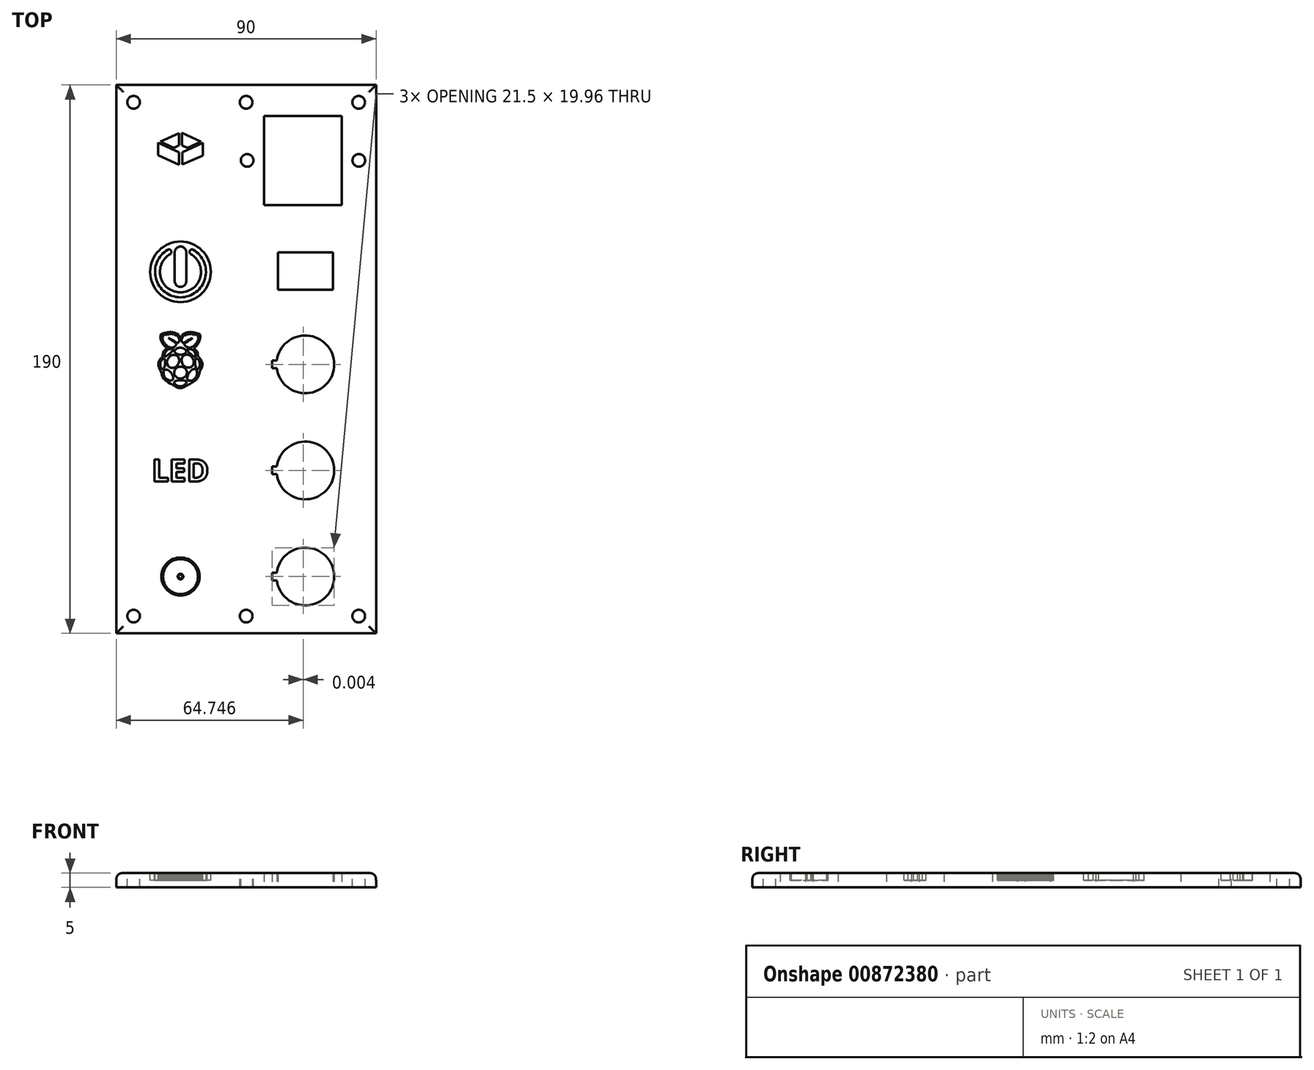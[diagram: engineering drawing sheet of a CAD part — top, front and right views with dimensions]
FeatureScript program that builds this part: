
annotation { "Feature Type Name" : "Feature", "Feature Type Description" : "" }
export const myFeature = defineFeature(function(context is Context, id is Id, definition is map)
    precondition{}
    {
        {
            var Q0;
            Q0=qCreatedBy(makeId("Top.planeOp"),FACE);
            var sketch = newSketch(context, id + "F0", { "sketchPlane" : qUnion([Q0])});
            skLineSegment(sketch, "E0.bottom", {"start": v(-22.25, -95) * mm, "end": v(-22.25, 95) * mm});
            skLineSegment(sketch, "E0.top", {"start": v(67.75, -95) * mm, "end": v(67.75, 95) * mm});
            skLineSegment(sketch, "E0.left", {"start": v(-22.25, -95) * mm, "end": v(67.75, -95) * mm});
            skLineSegment(sketch, "E0.right", {"start": v(-22.25, 95) * mm, "end": v(67.75, 95) * mm});
            skPoint(sketch, "E0.middle", {"position": v(31.26, -2.25) * mm});
            skLineSegment(sketch, "E1.bottom", {"start": v(55.89, 53.44) * mm, "end": v(29, 53.44) * mm});
            skLineSegment(sketch, "E1.top", {"start": v(55.89, 84.3) * mm, "end": v(29, 84.3) * mm});
            skLineSegment(sketch, "E1.left", {"start": v(55.89, 53.44) * mm, "end": v(55.89, 84.3) * mm});
            skLineSegment(sketch, "E1.right", {"start": v(29, 53.44) * mm, "end": v(29, 84.3) * mm});
            skLineSegment(sketch, "E2.bottom", {"start": v(33.81, 24.03) * mm, "end": v(33.81, 36.97) * mm});
            skLineSegment(sketch, "E2.top", {"start": v(52.81, 24.03) * mm, "end": v(52.81, 36.97) * mm});
            skLineSegment(sketch, "E2.left", {"start": v(33.81, 24.03) * mm, "end": v(52.81, 24.03) * mm});
            skLineSegment(sketch, "E2.right", {"start": v(33.81, 36.97) * mm, "end": v(52.81, 36.97) * mm});
            skPoint(sketch, "E3", {"position": v(61.79, 68.87) * mm});
            skPoint(sketch, "E4.endSnap0", {"position": v(42.44, 53.44) * mm});
            skPoint(sketch, "E5.MirrorP", {"position": v(23.1, 68.87) * mm});
            skArc(sketch, "E6", {"start": v(33.34, -3.11) * mm, "mid": v(53.25, -1.79) * mm, "end": v(33.34, -0.46) * mm});
            skLineSegment(sketch, "E7.top", {"start": v(33.34, -3.11) * mm, "end": v(31.75, -3.11) * mm});
            skLineSegment(sketch, "E8.MirrorCS", {"start": v(33.34, -0.46) * mm, "end": v(31.75, -0.46) * mm});
            skPoint(sketch, "E9.orphan", {"position": v(33.34, -0.46) * mm});
            skPoint(sketch, "E10.orphan", {"position": v(31.75, -0.46) * mm});
            skPoint(sketch, "E7.right.start.orphan", {"position": v(31.75, -1.79) * mm});
            skLineSegment(sketch, "E11", {"start": v(31.75, -0.46) * mm, "end": v(31.75, -3.11) * mm});
            skArc(sketch, "E12", {"start": v(33.34, -39.87) * mm, "mid": v(53.25, -38.54) * mm, "end": v(33.34, -37.22) * mm});
            skLineSegment(sketch, "E13.top", {"start": v(33.34, -39.87) * mm, "end": v(31.75, -39.87) * mm});
            skLineSegment(sketch, "E14.MirrorCS", {"start": v(33.34, -37.22) * mm, "end": v(31.75, -37.22) * mm});
            skLineSegment(sketch, "E15", {"start": v(31.75, -37.22) * mm, "end": v(31.75, -39.87) * mm});
            skArc(sketch, "E16", {"start": v(33.33, -76.62) * mm, "mid": v(53.25, -75.3) * mm, "end": v(33.33, -73.97) * mm});
            skLineSegment(sketch, "E17.top", {"start": v(33.33, -76.62) * mm, "end": v(31.75, -76.62) * mm});
            skLineSegment(sketch, "E18.MirrorCS", {"start": v(33.33, -73.97) * mm, "end": v(31.75, -73.97) * mm});
            skLineSegment(sketch, "E19", {"start": v(31.75, -73.97) * mm, "end": v(31.75, -76.62) * mm});
            skSolve(sketch);
        }
        {
            var Q0;
            Q0 = qSketchRegion(id + "F0", true);
            extrude(context, id + "F1", {"entities" : qUnion([Q0]), "depth" : 5 * mm, "offsetDistance" : 25 * mm});
        }
        {
            var Q0;
            Q0=makeQuery(id+"F1.opExtrude","CAP_FACE",FACE,{"disambiguationData":[OSD([sQuery(id+"F0.wireOp",EDGE,"E0.bottom"),sQuery(id+"F0.wireOp",EDGE,"E0.top"),sQuery(id+"F0.wireOp",EDGE,"E0.left"),sQuery(id+"F0.wireOp",EDGE,"E0.right"),sQuery(id+"F0.wireOp",EDGE,"E1.bottom"),sQuery(id+"F0.wireOp",EDGE,"E1.top"),sQuery(id+"F0.wireOp",EDGE,"E1.left"),sQuery(id+"F0.wireOp",EDGE,"E1.right"),sQuery(id+"F0.wireOp",EDGE,"E2.bottom"),sQuery(id+"F0.wireOp",EDGE,"E2.top"),sQuery(id+"F0.wireOp",EDGE,"E2.left"),sQuery(id+"F0.wireOp",EDGE,"E2.right"),sQuery(id+"F0.wireOp",EDGE,"E6"),sQuery(id+"F0.wireOp",EDGE,"E7.top"),sQuery(id+"F0.wireOp",EDGE,"E8.MirrorCS"),sQuery(id+"F0.wireOp",EDGE,"E11"),sQuery(id+"F0.wireOp",EDGE,"E12"),sQuery(id+"F0.wireOp",EDGE,"E13.top"),sQuery(id+"F0.wireOp",EDGE,"E14.MirrorCS"),sQuery(id+"F0.wireOp",EDGE,"E15"),sQuery(id+"F0.wireOp",EDGE,"E16"),sQuery(id+"F0.wireOp",EDGE,"E17.top"),sQuery(id+"F0.wireOp",EDGE,"E18.MirrorCS"),sQuery(id+"F0.wireOp",EDGE,"E19")])],"isStart":false});
            var sketch = newSketch(context, id + "F2", { "sketchPlane" : qUnion([Q0])});
            skPoint(sketch, "E20", {"position": v(61.79, 68.87) * mm});
            skPoint(sketch, "E21.MirrorP", {"position": v(23.1, 68.87) * mm});
            skCircle(sketch, "E22", {"center": v(0, 30.27) * mm, "radius": 11.5 * mm});
            skCircle(sketch, "E23", {"center": v(0, 30.27) * mm, "radius": 10.5 * mm});
            skArc(sketch, "E24", {"start": v(-4.42, 37.91) * mm, "mid": v(0, 21.44) * mm, "end": v(4.42, 37.91) * mm});
            skArc(sketch, "E25", {"start": v(-3.56, 36.44) * mm, "mid": v(0, 23.15) * mm, "end": v(3.56, 36.44) * mm});
            skPoint(sketch, "E26.orphan", {"position": v(0, 31.77) * mm});
            skArc(sketch, "E27", {"start": v(-4.42, 37.91) * mm, "mid": v(-3.25, 37.6) * mm, "end": v(-3.56, 36.44) * mm});
            skArc(sketch, "E28", {"start": v(4.42, 37.91) * mm, "mid": v(3.25, 37.6) * mm, "end": v(3.56, 36.44) * mm});
            skLineSegment(sketch, "E29.left", {"start": v(-2, 37.03) * mm, "end": v(-2, 27.03) * mm});
            skLineSegment(sketch, "E30.MirrorCS", {"start": v(2, 37.03) * mm, "end": v(2, 27.03) * mm});
            skArc(sketch, "E31", {"start": v(-2, 37.03) * mm, "mid": v(0, 39.03) * mm, "end": v(2, 37.03) * mm});
            skArc(sketch, "E32", {"start": v(2, 27.03) * mm, "mid": v(0, 25.03) * mm, "end": v(-2, 27.03) * mm});
            skCircle(sketch, "E33", {"center": v(0, -75.3) * mm, "radius": 0.97 * mm});
            skCircle(sketch, "E34", {"center": v(0, -75.3) * mm, "radius": 0.68 * mm});
            skCircle(sketch, "E35", {"center": v(0, -75.3) * mm, "radius": 6.05 * mm});
            skLineSegment(sketch, "E36", {"start": v(-0.85, -75.76) * mm, "end": v(-4.24, -78.57) * mm});
            skArc(sketch, "E37", {"start": v(-4.24, -78.57) * mm, "mid": v(-4.24, -79.53) * mm, "end": v(-3.28, -79.53) * mm});
            skLineSegment(sketch, "E38", {"start": v(-3.28, -79.53) * mm, "end": v(-0.47, -76.14) * mm});
            skLineSegment(sketch, "E39", {"start": v(-0.85, -74.83) * mm, "end": v(-4.24, -72.01) * mm});
            skArc(sketch, "E40", {"start": v(-4.24, -72.01) * mm, "mid": v(-4.24, -71.05) * mm, "end": v(-3.28, -71.05) * mm});
            skLineSegment(sketch, "E41", {"start": v(-3.28, -71.05) * mm, "end": v(-0.47, -74.44) * mm});
            skLineSegment(sketch, "E42", {"start": v(0.47, -76.14) * mm, "end": v(3.28, -79.53) * mm});
            skArc(sketch, "E43", {"start": v(3.28, -79.53) * mm, "mid": v(4.24, -79.53) * mm, "end": v(4.24, -78.57) * mm});
            skLineSegment(sketch, "E44", {"start": v(4.24, -78.57) * mm, "end": v(0.85, -75.76) * mm});
            skLineSegment(sketch, "E45", {"start": v(0.85, -74.83) * mm, "end": v(4.24, -72.01) * mm});
            skArc(sketch, "E46", {"start": v(4.24, -72.01) * mm, "mid": v(4.24, -71.05) * mm, "end": v(3.28, -71.05) * mm});
            skLineSegment(sketch, "E47", {"start": v(3.28, -71.05) * mm, "end": v(0.47, -74.44) * mm});
            skCircle(sketch, "E48", {"center": v(0, -75.3) * mm, "radius": 6.34 * mm});
            skText(sketch, "E49", { "text": "LED", "fontName": "OpenSans-Bold.ttf"});
            skLineSegment(sketch, "E50", {"start": v(0.77, -9.9) * mm, "end": v(0.41, -9.96) * mm});
            skLineSegment(sketch, "E51", {"start": v(0.41, -9.96) * mm, "end": v(0.04, -9.98) * mm});
            skLineSegment(sketch, "E52", {"start": v(2.22, -9.1) * mm, "end": v(1.83, -9.4) * mm});
            skLineSegment(sketch, "E53", {"start": v(1.83, -9.4) * mm, "end": v(1.43, -9.65) * mm});
            skLineSegment(sketch, "E54", {"start": v(1.43, -9.65) * mm, "end": v(0.77, -9.9) * mm});
            skLineSegment(sketch, "E55", {"start": v(2.71, -8.8) * mm, "end": v(2.41, -8.95) * mm});
            skLineSegment(sketch, "E56", {"start": v(2.41, -8.95) * mm, "end": v(2.22, -9.1) * mm});
            skLineSegment(sketch, "E57", {"start": v(3.97, -8.09) * mm, "end": v(3.25, -8.54) * mm});
            skLineSegment(sketch, "E58", {"start": v(3.25, -8.54) * mm, "end": v(2.71, -8.8) * mm});
            skLineSegment(sketch, "E59", {"start": v(4.54, -7.73) * mm, "end": v(4.42, -7.8) * mm});
            skLineSegment(sketch, "E60", {"start": v(4.42, -7.8) * mm, "end": v(4.25, -7.9) * mm});
            skLineSegment(sketch, "E61", {"start": v(4.25, -7.9) * mm, "end": v(3.97, -8.09) * mm});
            skLineSegment(sketch, "E62", {"start": v(5.46, -7.06) * mm, "end": v(5.2, -7.3) * mm});
            skLineSegment(sketch, "E63", {"start": v(5.2, -7.3) * mm, "end": v(4.95, -7.5) * mm});
            skLineSegment(sketch, "E64", {"start": v(4.95, -7.5) * mm, "end": v(4.54, -7.73) * mm});
            skLineSegment(sketch, "E65", {"start": v(6.35, -5.42) * mm, "end": v(6.2, -5.93) * mm});
            skLineSegment(sketch, "E66", {"start": v(6.2, -5.93) * mm, "end": v(5.98, -6.4) * mm});
            skLineSegment(sketch, "E67", {"start": v(5.98, -6.4) * mm, "end": v(5.74, -6.74) * mm});
            skLineSegment(sketch, "E68", {"start": v(5.74, -6.74) * mm, "end": v(5.46, -7.06) * mm});
            skLineSegment(sketch, "E69", {"start": v(6.54, -4.76) * mm, "end": v(6.42, -5.15) * mm});
            skLineSegment(sketch, "E70", {"start": v(6.42, -5.15) * mm, "end": v(6.35, -5.42) * mm});
            skLineSegment(sketch, "E71", {"start": v(6.74, -4.12) * mm, "end": v(6.7, -4.26) * mm});
            skLineSegment(sketch, "E72", {"start": v(6.7, -4.26) * mm, "end": v(6.64, -4.45) * mm});
            skLineSegment(sketch, "E73", {"start": v(6.64, -4.45) * mm, "end": v(6.54, -4.76) * mm});
            skLineSegment(sketch, "E74", {"start": v(6.97, -3.64) * mm, "end": v(6.88, -3.78) * mm});
            skLineSegment(sketch, "E75", {"start": v(6.88, -3.78) * mm, "end": v(6.82, -3.9) * mm});
            skLineSegment(sketch, "E76", {"start": v(6.82, -3.9) * mm, "end": v(6.74, -4.12) * mm});
            skLineSegment(sketch, "E77", {"start": v(7.5, -2.58) * mm, "end": v(7.39, -2.89) * mm});
            skLineSegment(sketch, "E78", {"start": v(7.39, -2.89) * mm, "end": v(7.24, -3.2) * mm});
            skLineSegment(sketch, "E79", {"start": v(7.24, -3.2) * mm, "end": v(7.11, -3.44) * mm});
            skLineSegment(sketch, "E80", {"start": v(7.11, -3.44) * mm, "end": v(6.97, -3.64) * mm});
            skLineSegment(sketch, "E81", {"start": v(7.5, -1.16) * mm, "end": v(7.55, -1.53) * mm});
            skLineSegment(sketch, "E82", {"start": v(7.55, -1.53) * mm, "end": v(7.57, -1.97) * mm});
            skLineSegment(sketch, "E83", {"start": v(7.57, -1.97) * mm, "end": v(7.54, -2.3) * mm});
            skLineSegment(sketch, "E84", {"start": v(7.54, -2.3) * mm, "end": v(7.5, -2.58) * mm});
            skLineSegment(sketch, "E85", {"start": v(7.13, -0.28) * mm, "end": v(7.36, -0.76) * mm});
            skLineSegment(sketch, "E86", {"start": v(7.36, -0.76) * mm, "end": v(7.5, -1.16) * mm});
            skLineSegment(sketch, "E87", {"start": v(6.4, 0.55) * mm, "end": v(6.6, 0.38) * mm});
            skLineSegment(sketch, "E88", {"start": v(6.6, 0.38) * mm, "end": v(6.83, 0.13) * mm});
            skLineSegment(sketch, "E89", {"start": v(6.83, 0.13) * mm, "end": v(7, -0.08) * mm});
            skLineSegment(sketch, "E90", {"start": v(7, -0.08) * mm, "end": v(7.13, -0.28) * mm});
            skLineSegment(sketch, "E91", {"start": v(6.11, 1.25) * mm, "end": v(6.14, 0.96) * mm});
            skLineSegment(sketch, "E92", {"start": v(6.14, 0.96) * mm, "end": v(6.2, 0.76) * mm});
            skLineSegment(sketch, "E93", {"start": v(6.2, 0.76) * mm, "end": v(6.4, 0.55) * mm});
            skLineSegment(sketch, "E94", {"start": v(4.65, 3.74) * mm, "end": v(5.12, 3.4) * mm});
            skLineSegment(sketch, "E95", {"start": v(5.12, 3.4) * mm, "end": v(5.5, 3) * mm});
            skLineSegment(sketch, "E96", {"start": v(5.5, 3) * mm, "end": v(5.79, 2.54) * mm});
            skLineSegment(sketch, "E97", {"start": v(5.79, 2.54) * mm, "end": v(6.01, 1.93) * mm});
            skLineSegment(sketch, "E98", {"start": v(6.01, 1.93) * mm, "end": v(6.11, 1.25) * mm});
            skLineSegment(sketch, "E99", {"start": v(4.5, 3.84) * mm, "end": v(4.65, 3.74) * mm});
            skLineSegment(sketch, "E100", {"start": v(4.69, 3.93) * mm, "end": v(4.5, 3.84) * mm});
            skLineSegment(sketch, "E101", {"start": v(5.03, 4.27) * mm, "end": v(4.9, 4.06) * mm});
            skLineSegment(sketch, "E102", {"start": v(4.9, 4.06) * mm, "end": v(4.69, 3.93) * mm});
            skLineSegment(sketch, "E103", {"start": v(5.22, 4.4) * mm, "end": v(5.08, 4.32) * mm});
            skLineSegment(sketch, "E104", {"start": v(5.08, 4.32) * mm, "end": v(5.03, 4.27) * mm});
            skLineSegment(sketch, "E105", {"start": v(5.66, 4.82) * mm, "end": v(5.59, 4.67) * mm});
            skLineSegment(sketch, "E106", {"start": v(5.59, 4.67) * mm, "end": v(5.47, 4.54) * mm});
            skLineSegment(sketch, "E107", {"start": v(5.47, 4.54) * mm, "end": v(5.22, 4.4) * mm});
            skLineSegment(sketch, "E108", {"start": v(5.79, 5) * mm, "end": v(5.7, 4.92) * mm});
            skLineSegment(sketch, "E109", {"start": v(5.7, 4.92) * mm, "end": v(5.66, 4.82) * mm});
            skLineSegment(sketch, "E110", {"start": v(6.2, 5.54) * mm, "end": v(6.13, 5.37) * mm});
            skLineSegment(sketch, "E111", {"start": v(6.13, 5.37) * mm, "end": v(6.01, 5.2) * mm});
            skLineSegment(sketch, "E112", {"start": v(6.01, 5.2) * mm, "end": v(5.79, 5) * mm});
            skLineSegment(sketch, "E113", {"start": v(6.3, 5.75) * mm, "end": v(6.26, 5.71) * mm});
            skLineSegment(sketch, "E114", {"start": v(6.26, 5.71) * mm, "end": v(6.23, 5.66) * mm});
            skLineSegment(sketch, "E115", {"start": v(6.23, 5.66) * mm, "end": v(6.2, 5.54) * mm});
            skLineSegment(sketch, "E116", {"start": v(6.51, 6.2) * mm, "end": v(6.49, 6.06) * mm});
            skLineSegment(sketch, "E117", {"start": v(6.49, 6.06) * mm, "end": v(6.43, 5.9) * mm});
            skLineSegment(sketch, "E118", {"start": v(6.43, 5.9) * mm, "end": v(6.36, 5.8) * mm});
            skLineSegment(sketch, "E119", {"start": v(6.36, 5.8) * mm, "end": v(6.3, 5.75) * mm});
            skLineSegment(sketch, "E120", {"start": v(6.63, 6.52) * mm, "end": v(6.53, 6.34) * mm});
            skLineSegment(sketch, "E121", {"start": v(6.53, 6.34) * mm, "end": v(6.51, 6.2) * mm});
            skLineSegment(sketch, "E122", {"start": v(6.76, 7.01) * mm, "end": v(6.74, 6.75) * mm});
            skLineSegment(sketch, "E123", {"start": v(6.74, 6.75) * mm, "end": v(6.63, 6.52) * mm});
            skLineSegment(sketch, "E124", {"start": v(6.82, 7.26) * mm, "end": v(6.76, 7.1) * mm});
            skLineSegment(sketch, "E125", {"start": v(6.76, 7.1) * mm, "end": v(6.76, 7.01) * mm});
            skLineSegment(sketch, "E126", {"start": v(6.84, 7.8) * mm, "end": v(6.9, 7.5) * mm});
            skLineSegment(sketch, "E127", {"start": v(6.9, 7.5) * mm, "end": v(6.82, 7.26) * mm});
            skLineSegment(sketch, "E128", {"start": v(6.8, 8) * mm, "end": v(6.8, 7.9) * mm});
            skLineSegment(sketch, "E129", {"start": v(6.8, 7.9) * mm, "end": v(6.84, 7.8) * mm});
            skLineSegment(sketch, "E130", {"start": v(6.77, 8.53) * mm, "end": v(6.82, 8.4) * mm});
            skLineSegment(sketch, "E131", {"start": v(6.82, 8.4) * mm, "end": v(6.84, 8.24) * mm});
            skLineSegment(sketch, "E132", {"start": v(6.84, 8.24) * mm, "end": v(6.8, 8) * mm});
            skLineSegment(sketch, "E133", {"start": v(6.28, 8.76) * mm, "end": v(6.6, 8.68) * mm});
            skLineSegment(sketch, "E134", {"start": v(6.6, 8.68) * mm, "end": v(6.77, 8.53) * mm});
            skLineSegment(sketch, "E135", {"start": v(6.07, 8.83) * mm, "end": v(6.17, 8.77) * mm});
            skLineSegment(sketch, "E136", {"start": v(6.17, 8.77) * mm, "end": v(6.28, 8.76) * mm});
            skLineSegment(sketch, "E137", {"start": v(5.5, 9.05) * mm, "end": v(5.87, 8.97) * mm});
            skLineSegment(sketch, "E138", {"start": v(5.87, 8.97) * mm, "end": v(6.07, 8.83) * mm});
            skLineSegment(sketch, "E139", {"start": v(5.18, 9.11) * mm, "end": v(5.23, 9.08) * mm});
            skLineSegment(sketch, "E140", {"start": v(5.23, 9.08) * mm, "end": v(5.3, 9.07) * mm});
            skLineSegment(sketch, "E141", {"start": v(5.3, 9.07) * mm, "end": v(5.5, 9.05) * mm});
            skLineSegment(sketch, "E142", {"start": v(4.74, 9.25) * mm, "end": v(5.01, 9.2) * mm});
            skLineSegment(sketch, "E143", {"start": v(5.01, 9.2) * mm, "end": v(5.18, 9.11) * mm});
            skLineSegment(sketch, "E144", {"start": v(4.49, 9.31) * mm, "end": v(4.63, 9.26) * mm});
            skLineSegment(sketch, "E145", {"start": v(4.63, 9.26) * mm, "end": v(4.74, 9.25) * mm});
            skLineSegment(sketch, "E146", {"start": v(3.87, 9.35) * mm, "end": v(4.03, 9.38) * mm});
            skLineSegment(sketch, "E147", {"start": v(4.03, 9.38) * mm, "end": v(4.22, 9.38) * mm});
            skLineSegment(sketch, "E148", {"start": v(4.22, 9.38) * mm, "end": v(4.37, 9.35) * mm});
            skLineSegment(sketch, "E149", {"start": v(4.37, 9.35) * mm, "end": v(4.49, 9.31) * mm});
            skLineSegment(sketch, "E150", {"start": v(3.7, 9.36) * mm, "end": v(3.8, 9.33) * mm});
            skLineSegment(sketch, "E151", {"start": v(3.8, 9.33) * mm, "end": v(3.87, 9.35) * mm});
            skLineSegment(sketch, "E152", {"start": v(3.11, 9.36) * mm, "end": v(3.27, 9.4) * mm});
            skLineSegment(sketch, "E153", {"start": v(3.27, 9.4) * mm, "end": v(3.45, 9.4) * mm});
            skLineSegment(sketch, "E154", {"start": v(3.45, 9.4) * mm, "end": v(3.59, 9.4) * mm});
            skLineSegment(sketch, "E155", {"start": v(3.59, 9.4) * mm, "end": v(3.7, 9.36) * mm});
            skLineSegment(sketch, "E156", {"start": v(2.74, 9.31) * mm, "end": v(2.98, 9.32) * mm});
            skLineSegment(sketch, "E157", {"start": v(2.98, 9.32) * mm, "end": v(3.11, 9.36) * mm});
            skLineSegment(sketch, "E158", {"start": v(2.34, 9.24) * mm, "end": v(2.53, 9.3) * mm});
            skLineSegment(sketch, "E159", {"start": v(2.53, 9.3) * mm, "end": v(2.74, 9.31) * mm});
            skLineSegment(sketch, "E160", {"start": v(2.07, 9.17) * mm, "end": v(2.21, 9.18) * mm});
            skLineSegment(sketch, "E161", {"start": v(2.21, 9.18) * mm, "end": v(2.34, 9.24) * mm});
            skLineSegment(sketch, "E162", {"start": v(1.52, 8.97) * mm, "end": v(1.82, 9.15) * mm});
            skLineSegment(sketch, "E163", {"start": v(1.82, 9.15) * mm, "end": v(2.07, 9.17) * mm});
            skLineSegment(sketch, "E164", {"start": v(1.23, 8.83) * mm, "end": v(1.38, 8.86) * mm});
            skLineSegment(sketch, "E165", {"start": v(1.38, 8.86) * mm, "end": v(1.52, 8.97) * mm});
            skLineSegment(sketch, "E166", {"start": v(0.06, 7.52) * mm, "end": v(0.35, 8.06) * mm});
            skLineSegment(sketch, "E167", {"start": v(0.35, 8.06) * mm, "end": v(0.7, 8.51) * mm});
            skLineSegment(sketch, "E168", {"start": v(0.7, 8.51) * mm, "end": v(1.02, 8.76) * mm});
            skLineSegment(sketch, "E169", {"start": v(1.02, 8.76) * mm, "end": v(1.23, 8.83) * mm});
            skLineSegment(sketch, "E170", {"start": v(-0.07, 7.35) * mm, "end": v(-0.07, 7.32) * mm});
            skLineSegment(sketch, "E171", {"start": v(-0.07, 7.32) * mm, "end": v(-0.06, 7.3) * mm});
            skLineSegment(sketch, "E172", {"start": v(-0.06, 7.3) * mm, "end": v(-0.06, 7.3) * mm});
            skLineSegment(sketch, "E173", {"start": v(-0.06, 7.3) * mm, "end": v(-0.05, 7.3) * mm});
            skLineSegment(sketch, "E174", {"start": v(-0.05, 7.3) * mm, "end": v(0, 7.4) * mm});
            skLineSegment(sketch, "E175", {"start": v(0, 7.4) * mm, "end": v(0.06, 7.52) * mm});
            skLineSegment(sketch, "E176", {"start": v(-0.61, 8.32) * mm, "end": v(-0.5, 8.16) * mm});
            skLineSegment(sketch, "E177", {"start": v(-0.5, 8.16) * mm, "end": v(-0.37, 7.95) * mm});
            skLineSegment(sketch, "E178", {"start": v(-0.37, 7.95) * mm, "end": v(-0.24, 7.72) * mm});
            skLineSegment(sketch, "E179", {"start": v(-0.24, 7.72) * mm, "end": v(-0.11, 7.46) * mm});
            skLineSegment(sketch, "E180", {"start": v(-0.11, 7.46) * mm, "end": v(-0.08, 7.39) * mm});
            skLineSegment(sketch, "E181", {"start": v(-0.08, 7.39) * mm, "end": v(-0.07, 7.35) * mm});
            skLineSegment(sketch, "E182", {"start": v(-1.32, 8.83) * mm, "end": v(-1.15, 8.78) * mm});
            skLineSegment(sketch, "E183", {"start": v(-1.15, 8.78) * mm, "end": v(-0.95, 8.65) * mm});
            skLineSegment(sketch, "E184", {"start": v(-0.95, 8.65) * mm, "end": v(-0.61, 8.32) * mm});
            skLineSegment(sketch, "E185", {"start": v(-1.6, 8.97) * mm, "end": v(-1.5, 8.9) * mm});
            skLineSegment(sketch, "E186", {"start": v(-1.5, 8.9) * mm, "end": v(-1.44, 8.85) * mm});
            skLineSegment(sketch, "E187", {"start": v(-1.44, 8.85) * mm, "end": v(-1.32, 8.83) * mm});
            skLineSegment(sketch, "E188", {"start": v(-2.15, 9.17) * mm, "end": v(-1.84, 9.13) * mm});
            skLineSegment(sketch, "E189", {"start": v(-1.84, 9.13) * mm, "end": v(-1.6, 8.97) * mm});
            skLineSegment(sketch, "E190", {"start": v(-2.42, 9.24) * mm, "end": v(-2.25, 9.17) * mm});
            skLineSegment(sketch, "E191", {"start": v(-2.25, 9.17) * mm, "end": v(-2.15, 9.17) * mm});
            skLineSegment(sketch, "E192", {"start": v(-2.8, 9.3) * mm, "end": v(-2.67, 9.31) * mm});
            skLineSegment(sketch, "E193", {"start": v(-2.67, 9.31) * mm, "end": v(-2.58, 9.3) * mm});
            skLineSegment(sketch, "E194", {"start": v(-2.58, 9.3) * mm, "end": v(-2.42, 9.24) * mm});
            skLineSegment(sketch, "E195", {"start": v(-3.16, 9.35) * mm, "end": v(-2.99, 9.3) * mm});
            skLineSegment(sketch, "E196", {"start": v(-2.99, 9.3) * mm, "end": v(-2.8, 9.3) * mm});
            skLineSegment(sketch, "E197", {"start": v(-3.77, 9.36) * mm, "end": v(-3.63, 9.4) * mm});
            skLineSegment(sketch, "E198", {"start": v(-3.63, 9.4) * mm, "end": v(-3.44, 9.4) * mm});
            skLineSegment(sketch, "E199", {"start": v(-3.44, 9.4) * mm, "end": v(-3.16, 9.35) * mm});
            skLineSegment(sketch, "E200", {"start": v(-3.97, 9.35) * mm, "end": v(-3.86, 9.33) * mm});
            skLineSegment(sketch, "E201", {"start": v(-3.86, 9.33) * mm, "end": v(-3.77, 9.36) * mm});
            skLineSegment(sketch, "E202", {"start": v(-4.6, 9.3) * mm, "end": v(-4.43, 9.35) * mm});
            skLineSegment(sketch, "E203", {"start": v(-4.43, 9.35) * mm, "end": v(-4.25, 9.38) * mm});
            skLineSegment(sketch, "E204", {"start": v(-4.25, 9.38) * mm, "end": v(-4.1, 9.37) * mm});
            skLineSegment(sketch, "E205", {"start": v(-4.1, 9.37) * mm, "end": v(-3.97, 9.35) * mm});
            skLineSegment(sketch, "E206", {"start": v(-4.8, 9.24) * mm, "end": v(-4.68, 9.26) * mm});
            skLineSegment(sketch, "E207", {"start": v(-4.68, 9.26) * mm, "end": v(-4.6, 9.3) * mm});
            skLineSegment(sketch, "E208", {"start": v(-5.24, 9.12) * mm, "end": v(-5, 9.22) * mm});
            skLineSegment(sketch, "E209", {"start": v(-5, 9.22) * mm, "end": v(-4.8, 9.24) * mm});
            skLineSegment(sketch, "E210", {"start": v(-5.52, 9.05) * mm, "end": v(-5.34, 9.07) * mm});
            skLineSegment(sketch, "E211", {"start": v(-5.34, 9.07) * mm, "end": v(-5.24, 9.12) * mm});
            skLineSegment(sketch, "E212", {"start": v(-6.1, 8.88) * mm, "end": v(-5.8, 9.02) * mm});
            skLineSegment(sketch, "E213", {"start": v(-5.8, 9.02) * mm, "end": v(-5.52, 9.05) * mm});
            skLineSegment(sketch, "E214", {"start": v(-6.38, 8.76) * mm, "end": v(-6.22, 8.8) * mm});
            skLineSegment(sketch, "E215", {"start": v(-6.22, 8.8) * mm, "end": v(-6.1, 8.88) * mm});
            skLineSegment(sketch, "E216", {"start": v(-6.86, 8.53) * mm, "end": v(-6.76, 8.63) * mm});
            skLineSegment(sketch, "E217", {"start": v(-6.76, 8.63) * mm, "end": v(-6.63, 8.7) * mm});
            skLineSegment(sketch, "E218", {"start": v(-6.63, 8.7) * mm, "end": v(-6.38, 8.76) * mm});
            skLineSegment(sketch, "E219", {"start": v(-6.9, 8) * mm, "end": v(-6.92, 8.15) * mm});
            skLineSegment(sketch, "E220", {"start": v(-6.92, 8.15) * mm, "end": v(-6.92, 8.31) * mm});
            skLineSegment(sketch, "E221", {"start": v(-6.92, 8.31) * mm, "end": v(-6.86, 8.53) * mm});
            skLineSegment(sketch, "E222", {"start": v(-6.92, 7.79) * mm, "end": v(-6.88, 7.92) * mm});
            skLineSegment(sketch, "E223", {"start": v(-6.88, 7.92) * mm, "end": v(-6.9, 8) * mm});
            skLineSegment(sketch, "E224", {"start": v(-6.9, 7.27) * mm, "end": v(-6.98, 7.57) * mm});
            skLineSegment(sketch, "E225", {"start": v(-6.98, 7.57) * mm, "end": v(-6.92, 7.79) * mm});
            skLineSegment(sketch, "E226", {"start": v(-6.84, 7) * mm, "end": v(-6.85, 7.13) * mm});
            skLineSegment(sketch, "E227", {"start": v(-6.85, 7.13) * mm, "end": v(-6.9, 7.27) * mm});
            skLineSegment(sketch, "E228", {"start": v(-6.7, 6.5) * mm, "end": v(-6.83, 6.8) * mm});
            skLineSegment(sketch, "E229", {"start": v(-6.83, 6.8) * mm, "end": v(-6.84, 7) * mm});
            skLineSegment(sketch, "E230", {"start": v(-6.6, 6.23) * mm, "end": v(-6.63, 6.38) * mm});
            skLineSegment(sketch, "E231", {"start": v(-6.63, 6.38) * mm, "end": v(-6.7, 6.5) * mm});
            skLineSegment(sketch, "E232", {"start": v(-6.4, 5.78) * mm, "end": v(-6.56, 6.02) * mm});
            skLineSegment(sketch, "E233", {"start": v(-6.56, 6.02) * mm, "end": v(-6.6, 6.23) * mm});
            skLineSegment(sketch, "E234", {"start": v(-6.27, 5.57) * mm, "end": v(-6.3, 5.68) * mm});
            skLineSegment(sketch, "E235", {"start": v(-6.3, 5.68) * mm, "end": v(-6.4, 5.78) * mm});
            skLineSegment(sketch, "E236", {"start": v(-5.82, 4.97) * mm, "end": v(-6, 5.1) * mm});
            skLineSegment(sketch, "E237", {"start": v(-6, 5.1) * mm, "end": v(-6.16, 5.29) * mm});
            skLineSegment(sketch, "E238", {"start": v(-6.16, 5.29) * mm, "end": v(-6.24, 5.44) * mm});
            skLineSegment(sketch, "E239", {"start": v(-6.24, 5.44) * mm, "end": v(-6.27, 5.57) * mm});
            skLineSegment(sketch, "E240", {"start": v(-5.75, 4.88) * mm, "end": v(-5.78, 4.93) * mm});
            skLineSegment(sketch, "E241", {"start": v(-5.78, 4.93) * mm, "end": v(-5.82, 4.97) * mm});
            skLineSegment(sketch, "E242", {"start": v(-5.24, 4.37) * mm, "end": v(-5.44, 4.46) * mm});
            skLineSegment(sketch, "E243", {"start": v(-5.44, 4.46) * mm, "end": v(-5.62, 4.61) * mm});
            skLineSegment(sketch, "E244", {"start": v(-5.62, 4.61) * mm, "end": v(-5.72, 4.75) * mm});
            skLineSegment(sketch, "E245", {"start": v(-5.72, 4.75) * mm, "end": v(-5.75, 4.88) * mm});
            skLineSegment(sketch, "E246", {"start": v(-5.09, 4.21) * mm, "end": v(-5.16, 4.33) * mm});
            skLineSegment(sketch, "E247", {"start": v(-5.16, 4.33) * mm, "end": v(-5.24, 4.37) * mm});
            skLineSegment(sketch, "E248", {"start": v(-4.65, 3.88) * mm, "end": v(-4.8, 3.93) * mm});
            skLineSegment(sketch, "E249", {"start": v(-4.8, 3.93) * mm, "end": v(-4.94, 4.03) * mm});
            skLineSegment(sketch, "E250", {"start": v(-4.94, 4.03) * mm, "end": v(-5.09, 4.21) * mm});
            skLineSegment(sketch, "E251", {"start": v(-4.84, 3.67) * mm, "end": v(-4.66, 3.8) * mm});
            skLineSegment(sketch, "E252", {"start": v(-4.66, 3.8) * mm, "end": v(-4.6, 3.84) * mm});
            skLineSegment(sketch, "E253", {"start": v(-4.6, 3.84) * mm, "end": v(-4.6, 3.85) * mm});
            skLineSegment(sketch, "E254", {"start": v(-4.6, 3.85) * mm, "end": v(-4.6, 3.86) * mm});
            skLineSegment(sketch, "E255", {"start": v(-4.6, 3.86) * mm, "end": v(-4.62, 3.87) * mm});
            skLineSegment(sketch, "E256", {"start": v(-4.62, 3.87) * mm, "end": v(-4.65, 3.88) * mm});
            skLineSegment(sketch, "E257", {"start": v(-5.76, 2.74) * mm, "end": v(-5.57, 3) * mm});
            skLineSegment(sketch, "E258", {"start": v(-5.57, 3) * mm, "end": v(-5.3, 3.29) * mm});
            skLineSegment(sketch, "E259", {"start": v(-5.3, 3.29) * mm, "end": v(-5.07, 3.5) * mm});
            skLineSegment(sketch, "E260", {"start": v(-5.07, 3.5) * mm, "end": v(-4.84, 3.67) * mm});
            skLineSegment(sketch, "E261", {"start": v(-6.2, 1.2) * mm, "end": v(-6.15, 1.68) * mm});
            skLineSegment(sketch, "E262", {"start": v(-6.15, 1.68) * mm, "end": v(-6.04, 2.13) * mm});
            skLineSegment(sketch, "E263", {"start": v(-6.04, 2.13) * mm, "end": v(-5.76, 2.74) * mm});
            skLineSegment(sketch, "E264", {"start": v(-6.5, 0.54) * mm, "end": v(-6.34, 0.67) * mm});
            skLineSegment(sketch, "E265", {"start": v(-6.34, 0.67) * mm, "end": v(-6.26, 0.82) * mm});
            skLineSegment(sketch, "E266", {"start": v(-6.26, 0.82) * mm, "end": v(-6.22, 0.98) * mm});
            skLineSegment(sketch, "E267", {"start": v(-6.22, 0.98) * mm, "end": v(-6.2, 1.2) * mm});
            skLineSegment(sketch, "E268", {"start": v(-7.58, -1.2) * mm, "end": v(-7.38, -0.61) * mm});
            skLineSegment(sketch, "E269", {"start": v(-7.38, -0.61) * mm, "end": v(-7.09, -0.1) * mm});
            skLineSegment(sketch, "E270", {"start": v(-7.09, -0.1) * mm, "end": v(-6.81, 0.26) * mm});
            skLineSegment(sketch, "E271", {"start": v(-6.81, 0.26) * mm, "end": v(-6.5, 0.54) * mm});
            skLineSegment(sketch, "E272", {"start": v(-7.58, -2.56) * mm, "end": v(-7.64, -2.2) * mm});
            skLineSegment(sketch, "E273", {"start": v(-7.64, -2.2) * mm, "end": v(-7.65, -1.8) * mm});
            skLineSegment(sketch, "E274", {"start": v(-7.65, -1.8) * mm, "end": v(-7.63, -1.48) * mm});
            skLineSegment(sketch, "E275", {"start": v(-7.63, -1.48) * mm, "end": v(-7.58, -1.2) * mm});
            skLineSegment(sketch, "E276", {"start": v(-7.07, -3.62) * mm, "end": v(-7.4, -3.04) * mm});
            skLineSegment(sketch, "E277", {"start": v(-7.4, -3.04) * mm, "end": v(-7.58, -2.56) * mm});
            skLineSegment(sketch, "E278", {"start": v(-6.8, -4.17) * mm, "end": v(-6.86, -4) * mm});
            skLineSegment(sketch, "E279", {"start": v(-6.86, -4) * mm, "end": v(-6.92, -3.85) * mm});
            skLineSegment(sketch, "E280", {"start": v(-6.92, -3.85) * mm, "end": v(-7.07, -3.62) * mm});
            skLineSegment(sketch, "E281", {"start": v(-6.61, -4.79) * mm, "end": v(-6.73, -4.43) * mm});
            skLineSegment(sketch, "E282", {"start": v(-6.73, -4.43) * mm, "end": v(-6.8, -4.17) * mm});
            skLineSegment(sketch, "E283", {"start": v(-6.43, -5.42) * mm, "end": v(-6.47, -5.26) * mm});
            skLineSegment(sketch, "E284", {"start": v(-6.47, -5.26) * mm, "end": v(-6.52, -5.07) * mm});
            skLineSegment(sketch, "E285", {"start": v(-6.52, -5.07) * mm, "end": v(-6.61, -4.79) * mm});
            skLineSegment(sketch, "E286", {"start": v(-4.62, -7.73) * mm, "end": v(-5.1, -7.45) * mm});
            skLineSegment(sketch, "E287", {"start": v(-5.1, -7.45) * mm, "end": v(-5.53, -7.1) * mm});
            skLineSegment(sketch, "E288", {"start": v(-5.53, -7.1) * mm, "end": v(-5.9, -6.66) * mm});
            skLineSegment(sketch, "E289", {"start": v(-5.9, -6.66) * mm, "end": v(-6.22, -6.07) * mm});
            skLineSegment(sketch, "E290", {"start": v(-6.22, -6.07) * mm, "end": v(-6.43, -5.42) * mm});
            skLineSegment(sketch, "E291", {"start": v(-4.14, -8.03) * mm, "end": v(-4.42, -7.84) * mm});
            skLineSegment(sketch, "E292", {"start": v(-4.42, -7.84) * mm, "end": v(-4.62, -7.73) * mm});
            skLineSegment(sketch, "E293", {"start": v(-2.82, -8.78) * mm, "end": v(-3.17, -8.62) * mm});
            skLineSegment(sketch, "E294", {"start": v(-3.17, -8.62) * mm, "end": v(-3.56, -8.4) * mm});
            skLineSegment(sketch, "E295", {"start": v(-3.56, -8.4) * mm, "end": v(-4.14, -8.03) * mm});
            skLineSegment(sketch, "E296", {"start": v(-2.26, -9.12) * mm, "end": v(-2.52, -8.92) * mm});
            skLineSegment(sketch, "E297", {"start": v(-2.52, -8.92) * mm, "end": v(-2.65, -8.86) * mm});
            skLineSegment(sketch, "E298", {"start": v(-2.65, -8.86) * mm, "end": v(-2.82, -8.78) * mm});
            skLineSegment(sketch, "E299", {"start": v(-0.51, -9.98) * mm, "end": v(-1.04, -9.84) * mm});
            skLineSegment(sketch, "E300", {"start": v(-1.04, -9.84) * mm, "end": v(-1.55, -9.62) * mm});
            skLineSegment(sketch, "E301", {"start": v(-1.55, -9.62) * mm, "end": v(-1.93, -9.4) * mm});
            skLineSegment(sketch, "E302", {"start": v(-1.93, -9.4) * mm, "end": v(-2.26, -9.12) * mm});
            skLineSegment(sketch, "E303", {"start": v(0.04, -9.98) * mm, "end": v(-0.17, -9.98) * mm});
            skLineSegment(sketch, "E304", {"start": v(-0.17, -9.98) * mm, "end": v(-0.35, -9.98) * mm});
            skLineSegment(sketch, "E305", {"start": v(-0.35, -9.98) * mm, "end": v(-0.45, -9.98) * mm});
            skLineSegment(sketch, "E306", {"start": v(-0.45, -9.98) * mm, "end": v(-0.51, -9.98) * mm});
            skLineSegment(sketch, "E307", {"start": v(1.43, -8.89) * mm, "end": v(1, -9.13) * mm});
            skLineSegment(sketch, "E308", {"start": v(1, -9.13) * mm, "end": v(0.6, -9.29) * mm});
            skLineSegment(sketch, "E309", {"start": v(0.6, -9.29) * mm, "end": v(0.26, -9.36) * mm});
            skLineSegment(sketch, "E310", {"start": v(0.26, -9.36) * mm, "end": v(-0.09, -9.38) * mm});
            skLineSegment(sketch, "E311", {"start": v(-0.09, -9.38) * mm, "end": v(-0.43, -9.36) * mm});
            skLineSegment(sketch, "E312", {"start": v(-0.43, -9.36) * mm, "end": v(-0.63, -9.33) * mm});
            skLineSegment(sketch, "E313", {"start": v(-0.63, -9.33) * mm, "end": v(-1.06, -9.17) * mm});
            skLineSegment(sketch, "E314", {"start": v(-1.06, -9.17) * mm, "end": v(-1.47, -8.96) * mm});
            skLineSegment(sketch, "E315", {"start": v(-1.47, -8.96) * mm, "end": v(-1.82, -8.7) * mm});
            skLineSegment(sketch, "E316", {"start": v(-1.82, -8.7) * mm, "end": v(-2, -8.54) * mm});
            skLineSegment(sketch, "E317", {"start": v(-2, -8.54) * mm, "end": v(-2.13, -8.37) * mm});
            skLineSegment(sketch, "E318", {"start": v(-2.13, -8.37) * mm, "end": v(-2.22, -8.12) * mm});
            skLineSegment(sketch, "E319", {"start": v(-2.22, -8.12) * mm, "end": v(-2.18, -7.97) * mm});
            skLineSegment(sketch, "E320", {"start": v(-2.18, -7.97) * mm, "end": v(-2.08, -7.83) * mm});
            skLineSegment(sketch, "E321", {"start": v(-2.08, -7.83) * mm, "end": v(-1.94, -7.73) * mm});
            skLineSegment(sketch, "E322", {"start": v(-1.94, -7.73) * mm, "end": v(-1.75, -7.63) * mm});
            skLineSegment(sketch, "E323", {"start": v(-1.75, -7.63) * mm, "end": v(-1.3, -7.45) * mm});
            skLineSegment(sketch, "E324", {"start": v(-1.3, -7.45) * mm, "end": v(-0.81, -7.34) * mm});
            skLineSegment(sketch, "E325", {"start": v(-0.81, -7.34) * mm, "end": v(0.08, -7.27) * mm});
            skLineSegment(sketch, "E326", {"start": v(0.08, -7.27) * mm, "end": v(0.82, -7.32) * mm});
            skLineSegment(sketch, "E327", {"start": v(0.82, -7.32) * mm, "end": v(1.46, -7.47) * mm});
            skLineSegment(sketch, "E328", {"start": v(1.46, -7.47) * mm, "end": v(1.7, -7.57) * mm});
            skLineSegment(sketch, "E329", {"start": v(1.7, -7.57) * mm, "end": v(1.9, -7.7) * mm});
            skLineSegment(sketch, "E330", {"start": v(1.9, -7.7) * mm, "end": v(2.05, -7.82) * mm});
            skLineSegment(sketch, "E331", {"start": v(2.05, -7.82) * mm, "end": v(2.12, -7.96) * mm});
            skLineSegment(sketch, "E332", {"start": v(2.12, -7.96) * mm, "end": v(2.11, -8.07) * mm});
            skLineSegment(sketch, "E333", {"start": v(2.11, -8.07) * mm, "end": v(2.06, -8.21) * mm});
            skLineSegment(sketch, "E334", {"start": v(2.06, -8.21) * mm, "end": v(1.9, -8.46) * mm});
            skLineSegment(sketch, "E335", {"start": v(1.9, -8.46) * mm, "end": v(1.69, -8.68) * mm});
            skLineSegment(sketch, "E336", {"start": v(1.69, -8.68) * mm, "end": v(1.43, -8.89) * mm});
            skLineSegment(sketch, "E337", {"start": v(5.19, -6.43) * mm, "end": v(4.7, -6.91) * mm});
            skLineSegment(sketch, "E338", {"start": v(4.7, -6.91) * mm, "end": v(4.17, -7.25) * mm});
            skLineSegment(sketch, "E339", {"start": v(4.17, -7.25) * mm, "end": v(3.72, -7.41) * mm});
            skLineSegment(sketch, "E340", {"start": v(3.72, -7.41) * mm, "end": v(3.27, -7.46) * mm});
            skLineSegment(sketch, "E341", {"start": v(3.27, -7.46) * mm, "end": v(3.06, -7.45) * mm});
            skLineSegment(sketch, "E342", {"start": v(3.06, -7.45) * mm, "end": v(2.94, -7.43) * mm});
            skLineSegment(sketch, "E343", {"start": v(2.94, -7.43) * mm, "end": v(2.66, -7.32) * mm});
            skLineSegment(sketch, "E344", {"start": v(2.66, -7.32) * mm, "end": v(2.48, -7.15) * mm});
            skLineSegment(sketch, "E345", {"start": v(2.48, -7.15) * mm, "end": v(2.39, -6.96) * mm});
            skLineSegment(sketch, "E346", {"start": v(2.39, -6.96) * mm, "end": v(2.34, -6.7) * mm});
            skLineSegment(sketch, "E347", {"start": v(2.34, -6.7) * mm, "end": v(2.34, -6.37) * mm});
            skLineSegment(sketch, "E348", {"start": v(2.34, -6.37) * mm, "end": v(2.4, -6) * mm});
            skLineSegment(sketch, "E349", {"start": v(2.4, -6) * mm, "end": v(2.51, -5.61) * mm});
            skLineSegment(sketch, "E350", {"start": v(2.51, -5.61) * mm, "end": v(2.7, -5.15) * mm});
            skLineSegment(sketch, "E351", {"start": v(2.7, -5.15) * mm, "end": v(2.95, -4.72) * mm});
            skLineSegment(sketch, "E352", {"start": v(2.95, -4.72) * mm, "end": v(3.28, -4.33) * mm});
            skLineSegment(sketch, "E353", {"start": v(3.28, -4.33) * mm, "end": v(3.7, -3.93) * mm});
            skLineSegment(sketch, "E354", {"start": v(3.7, -3.93) * mm, "end": v(4.03, -3.67) * mm});
            skLineSegment(sketch, "E355", {"start": v(4.03, -3.67) * mm, "end": v(4.34, -3.48) * mm});
            skLineSegment(sketch, "E356", {"start": v(4.34, -3.48) * mm, "end": v(4.73, -3.34) * mm});
            skLineSegment(sketch, "E357", {"start": v(4.73, -3.34) * mm, "end": v(5.08, -3.35) * mm});
            skLineSegment(sketch, "E358", {"start": v(5.08, -3.35) * mm, "end": v(5.3, -3.45) * mm});
            skLineSegment(sketch, "E359", {"start": v(5.3, -3.45) * mm, "end": v(5.48, -3.63) * mm});
            skLineSegment(sketch, "E360", {"start": v(5.48, -3.63) * mm, "end": v(5.62, -3.93) * mm});
            skLineSegment(sketch, "E361", {"start": v(5.62, -3.93) * mm, "end": v(5.71, -4.3) * mm});
            skLineSegment(sketch, "E362", {"start": v(5.71, -4.3) * mm, "end": v(5.75, -4.72) * mm});
            skLineSegment(sketch, "E363", {"start": v(5.75, -4.72) * mm, "end": v(5.72, -5.21) * mm});
            skLineSegment(sketch, "E364", {"start": v(5.72, -5.21) * mm, "end": v(5.62, -5.67) * mm});
            skLineSegment(sketch, "E365", {"start": v(5.62, -5.67) * mm, "end": v(5.54, -5.89) * mm});
            skLineSegment(sketch, "E366", {"start": v(5.54, -5.89) * mm, "end": v(5.44, -6.07) * mm});
            skLineSegment(sketch, "E367", {"start": v(5.44, -6.07) * mm, "end": v(5.33, -6.23) * mm});
            skLineSegment(sketch, "E368", {"start": v(5.33, -6.23) * mm, "end": v(5.19, -6.43) * mm});
            skLineSegment(sketch, "E369", {"start": v(-2.57, -6.75) * mm, "end": v(-2.68, -7.09) * mm});
            skLineSegment(sketch, "E370", {"start": v(-2.68, -7.09) * mm, "end": v(-2.89, -7.3) * mm});
            skLineSegment(sketch, "E371", {"start": v(-2.89, -7.3) * mm, "end": v(-3.13, -7.37) * mm});
            skLineSegment(sketch, "E372", {"start": v(-3.13, -7.37) * mm, "end": v(-3.46, -7.4) * mm});
            skLineSegment(sketch, "E373", {"start": v(-3.46, -7.4) * mm, "end": v(-3.76, -7.38) * mm});
            skLineSegment(sketch, "E374", {"start": v(-3.76, -7.38) * mm, "end": v(-3.96, -7.34) * mm});
            skLineSegment(sketch, "E375", {"start": v(-3.96, -7.34) * mm, "end": v(-4.48, -7.1) * mm});
            skLineSegment(sketch, "E376", {"start": v(-4.48, -7.1) * mm, "end": v(-4.97, -6.75) * mm});
            skLineSegment(sketch, "E377", {"start": v(-4.97, -6.75) * mm, "end": v(-5.3, -6.42) * mm});
            skLineSegment(sketch, "E378", {"start": v(-5.3, -6.42) * mm, "end": v(-5.53, -6.06) * mm});
            skLineSegment(sketch, "E379", {"start": v(-5.53, -6.06) * mm, "end": v(-5.7, -5.63) * mm});
            skLineSegment(sketch, "E380", {"start": v(-5.7, -5.63) * mm, "end": v(-5.83, -5.17) * mm});
            skLineSegment(sketch, "E381", {"start": v(-5.83, -5.17) * mm, "end": v(-5.87, -4.83) * mm});
            skLineSegment(sketch, "E382", {"start": v(-5.87, -4.83) * mm, "end": v(-5.87, -4.53) * mm});
            skLineSegment(sketch, "E383", {"start": v(-5.87, -4.53) * mm, "end": v(-5.8, -4.16) * mm});
            skLineSegment(sketch, "E384", {"start": v(-5.8, -4.16) * mm, "end": v(-5.65, -3.9) * mm});
            skLineSegment(sketch, "E385", {"start": v(-5.65, -3.9) * mm, "end": v(-5.44, -3.72) * mm});
            skLineSegment(sketch, "E386", {"start": v(-5.44, -3.72) * mm, "end": v(-5.12, -3.63) * mm});
            skLineSegment(sketch, "E387", {"start": v(-5.12, -3.63) * mm, "end": v(-4.7, -3.68) * mm});
            skLineSegment(sketch, "E388", {"start": v(-4.7, -3.68) * mm, "end": v(-4.36, -3.82) * mm});
            skLineSegment(sketch, "E389", {"start": v(-4.36, -3.82) * mm, "end": v(-4, -4.04) * mm});
            skLineSegment(sketch, "E390", {"start": v(-4, -4.04) * mm, "end": v(-3.63, -4.32) * mm});
            skLineSegment(sketch, "E391", {"start": v(-3.63, -4.32) * mm, "end": v(-3.25, -4.7) * mm});
            skLineSegment(sketch, "E392", {"start": v(-3.25, -4.7) * mm, "end": v(-2.97, -5.1) * mm});
            skLineSegment(sketch, "E393", {"start": v(-2.97, -5.1) * mm, "end": v(-2.75, -5.58) * mm});
            skLineSegment(sketch, "E394", {"start": v(-2.75, -5.58) * mm, "end": v(-2.6, -6.07) * mm});
            skLineSegment(sketch, "E395", {"start": v(-2.6, -6.07) * mm, "end": v(-2.56, -6.44) * mm});
            skLineSegment(sketch, "E396", {"start": v(-2.56, -6.44) * mm, "end": v(-2.57, -6.75) * mm});
            skLineSegment(sketch, "E397", {"start": v(2.18, -5.1) * mm, "end": v(2.02, -5.51) * mm});
            skLineSegment(sketch, "E398", {"start": v(2.02, -5.51) * mm, "end": v(1.77, -5.88) * mm});
            skLineSegment(sketch, "E399", {"start": v(1.77, -5.88) * mm, "end": v(1.44, -6.2) * mm});
            skLineSegment(sketch, "E400", {"start": v(1.44, -6.2) * mm, "end": v(0.98, -6.49) * mm});
            skLineSegment(sketch, "E401", {"start": v(0.98, -6.49) * mm, "end": v(0.46, -6.65) * mm});
            skLineSegment(sketch, "E402", {"start": v(0.46, -6.65) * mm, "end": v(0.2, -6.68) * mm});
            skLineSegment(sketch, "E403", {"start": v(0.2, -6.68) * mm, "end": v(-0.1, -6.68) * mm});
            skLineSegment(sketch, "E404", {"start": v(-0.1, -6.68) * mm, "end": v(-0.32, -6.67) * mm});
            skLineSegment(sketch, "E405", {"start": v(-0.32, -6.67) * mm, "end": v(-0.51, -6.64) * mm});
            skLineSegment(sketch, "E406", {"start": v(-0.51, -6.64) * mm, "end": v(-1.1, -6.43) * mm});
            skLineSegment(sketch, "E407", {"start": v(-1.1, -6.43) * mm, "end": v(-1.59, -6.07) * mm});
            skLineSegment(sketch, "E408", {"start": v(-1.59, -6.07) * mm, "end": v(-1.9, -5.72) * mm});
            skLineSegment(sketch, "E409", {"start": v(-1.9, -5.72) * mm, "end": v(-2.1, -5.3) * mm});
            skLineSegment(sketch, "E410", {"start": v(-2.1, -5.3) * mm, "end": v(-2.18, -5.02) * mm});
            skLineSegment(sketch, "E411", {"start": v(-2.18, -5.02) * mm, "end": v(-2.21, -4.7) * mm});
            skLineSegment(sketch, "E412", {"start": v(-2.21, -4.7) * mm, "end": v(-2.21, -4.43) * mm});
            skLineSegment(sketch, "E413", {"start": v(-2.21, -4.43) * mm, "end": v(-2.19, -4.2) * mm});
            skLineSegment(sketch, "E414", {"start": v(-2.19, -4.2) * mm, "end": v(-2.06, -3.83) * mm});
            skLineSegment(sketch, "E415", {"start": v(-2.06, -3.83) * mm, "end": v(-1.85, -3.48) * mm});
            skLineSegment(sketch, "E416", {"start": v(-1.85, -3.48) * mm, "end": v(-1.56, -3.17) * mm});
            skLineSegment(sketch, "E417", {"start": v(-1.56, -3.17) * mm, "end": v(-1.15, -2.87) * mm});
            skLineSegment(sketch, "E418", {"start": v(-1.15, -2.87) * mm, "end": v(-0.68, -2.66) * mm});
            skLineSegment(sketch, "E419", {"start": v(-0.68, -2.66) * mm, "end": v(-0.26, -2.58) * mm});
            skLineSegment(sketch, "E420", {"start": v(-0.26, -2.58) * mm, "end": v(0.2, -2.58) * mm});
            skLineSegment(sketch, "E421", {"start": v(0.2, -2.58) * mm, "end": v(0.54, -2.63) * mm});
            skLineSegment(sketch, "E422", {"start": v(0.54, -2.63) * mm, "end": v(0.87, -2.73) * mm});
            skLineSegment(sketch, "E423", {"start": v(0.87, -2.73) * mm, "end": v(1.36, -3) * mm});
            skLineSegment(sketch, "E424", {"start": v(1.36, -3) * mm, "end": v(1.78, -3.39) * mm});
            skLineSegment(sketch, "E425", {"start": v(1.78, -3.39) * mm, "end": v(2.02, -3.75) * mm});
            skLineSegment(sketch, "E426", {"start": v(2.02, -3.75) * mm, "end": v(2.18, -4.14) * mm});
            skLineSegment(sketch, "E427", {"start": v(2.18, -4.14) * mm, "end": v(2.22, -4.4) * mm});
            skLineSegment(sketch, "E428", {"start": v(2.22, -4.4) * mm, "end": v(2.23, -4.7) * mm});
            skLineSegment(sketch, "E429", {"start": v(2.23, -4.7) * mm, "end": v(2.21, -4.92) * mm});
            skLineSegment(sketch, "E430", {"start": v(2.21, -4.92) * mm, "end": v(2.18, -5.1) * mm});
            skLineSegment(sketch, "E431", {"start": v(-5.4, -1.93) * mm, "end": v(-5.53, -2.52) * mm});
            skLineSegment(sketch, "E432", {"start": v(-5.53, -2.52) * mm, "end": v(-5.7, -3.02) * mm});
            skLineSegment(sketch, "E433", {"start": v(-5.7, -3.02) * mm, "end": v(-5.84, -3.3) * mm});
            skLineSegment(sketch, "E434", {"start": v(-5.84, -3.3) * mm, "end": v(-5.99, -3.5) * mm});
            skLineSegment(sketch, "E435", {"start": v(-5.99, -3.5) * mm, "end": v(-6.21, -3.57) * mm});
            skLineSegment(sketch, "E436", {"start": v(-6.21, -3.57) * mm, "end": v(-6.38, -3.5) * mm});
            skLineSegment(sketch, "E437", {"start": v(-6.38, -3.5) * mm, "end": v(-6.49, -3.4) * mm});
            skLineSegment(sketch, "E438", {"start": v(-6.49, -3.4) * mm, "end": v(-6.61, -3.23) * mm});
            skLineSegment(sketch, "E439", {"start": v(-6.61, -3.23) * mm, "end": v(-6.79, -2.93) * mm});
            skLineSegment(sketch, "E440", {"start": v(-6.79, -2.93) * mm, "end": v(-6.95, -2.51) * mm});
            skLineSegment(sketch, "E441", {"start": v(-6.95, -2.51) * mm, "end": v(-7.03, -2.07) * mm});
            skLineSegment(sketch, "E442", {"start": v(-7.03, -2.07) * mm, "end": v(-7.03, -1.61) * mm});
            skLineSegment(sketch, "E443", {"start": v(-7.03, -1.61) * mm, "end": v(-6.93, -1.1) * mm});
            skLineSegment(sketch, "E444", {"start": v(-6.93, -1.1) * mm, "end": v(-6.72, -0.63) * mm});
            skLineSegment(sketch, "E445", {"start": v(-6.72, -0.63) * mm, "end": v(-6.47, -0.28) * mm});
            skLineSegment(sketch, "E446", {"start": v(-6.47, -0.28) * mm, "end": v(-6.16, 0.01) * mm});
            skLineSegment(sketch, "E447", {"start": v(-6.16, 0.01) * mm, "end": v(-5.9, 0.18) * mm});
            skLineSegment(sketch, "E448", {"start": v(-5.9, 0.18) * mm, "end": v(-5.74, 0.23) * mm});
            skLineSegment(sketch, "E449", {"start": v(-5.74, 0.23) * mm, "end": v(-5.61, 0.2) * mm});
            skLineSegment(sketch, "E450", {"start": v(-5.61, 0.2) * mm, "end": v(-5.5, 0.1) * mm});
            skLineSegment(sketch, "E451", {"start": v(-5.5, 0.1) * mm, "end": v(-5.37, -0.16) * mm});
            skLineSegment(sketch, "E452", {"start": v(-5.37, -0.16) * mm, "end": v(-5.34, -0.34) * mm});
            skLineSegment(sketch, "E453", {"start": v(-5.34, -0.34) * mm, "end": v(-5.32, -0.6) * mm});
            skLineSegment(sketch, "E454", {"start": v(-5.32, -0.6) * mm, "end": v(-5.32, -1.08) * mm});
            skLineSegment(sketch, "E455", {"start": v(-5.32, -1.08) * mm, "end": v(-5.34, -1.53) * mm});
            skLineSegment(sketch, "E456", {"start": v(-5.34, -1.53) * mm, "end": v(-5.4, -1.93) * mm});
            skLineSegment(sketch, "E457", {"start": v(6.5, -2.88) * mm, "end": v(6.36, -3.14) * mm});
            skLineSegment(sketch, "E458", {"start": v(6.36, -3.14) * mm, "end": v(6.18, -3.37) * mm});
            skLineSegment(sketch, "E459", {"start": v(6.18, -3.37) * mm, "end": v(6.03, -3.5) * mm});
            skLineSegment(sketch, "E460", {"start": v(6.03, -3.5) * mm, "end": v(5.94, -3.54) * mm});
            skLineSegment(sketch, "E461", {"start": v(5.94, -3.54) * mm, "end": v(5.86, -3.52) * mm});
            skLineSegment(sketch, "E462", {"start": v(5.86, -3.52) * mm, "end": v(5.78, -3.48) * mm});
            skLineSegment(sketch, "E463", {"start": v(5.78, -3.48) * mm, "end": v(5.66, -3.37) * mm});
            skLineSegment(sketch, "E464", {"start": v(5.66, -3.37) * mm, "end": v(5.54, -3.2) * mm});
            skLineSegment(sketch, "E465", {"start": v(5.54, -3.2) * mm, "end": v(5.36, -2.82) * mm});
            skLineSegment(sketch, "E466", {"start": v(5.36, -2.82) * mm, "end": v(5.23, -2.38) * mm});
            skLineSegment(sketch, "E467", {"start": v(5.23, -2.38) * mm, "end": v(5.11, -1.85) * mm});
            skLineSegment(sketch, "E468", {"start": v(5.11, -1.85) * mm, "end": v(5.07, -1.52) * mm});
            skLineSegment(sketch, "E469", {"start": v(5.07, -1.52) * mm, "end": v(5.04, -1.15) * mm});
            skLineSegment(sketch, "E470", {"start": v(5.04, -1.15) * mm, "end": v(5.04, -0.77) * mm});
            skLineSegment(sketch, "E471", {"start": v(5.04, -0.77) * mm, "end": v(5.05, -0.38) * mm});
            skLineSegment(sketch, "E472", {"start": v(5.05, -0.38) * mm, "end": v(5.1, -0.12) * mm});
            skLineSegment(sketch, "E473", {"start": v(5.1, -0.12) * mm, "end": v(5.18, 0.06) * mm});
            skLineSegment(sketch, "E474", {"start": v(5.18, 0.06) * mm, "end": v(5.28, 0.2) * mm});
            skLineSegment(sketch, "E475", {"start": v(5.28, 0.2) * mm, "end": v(5.37, 0.27) * mm});
            skLineSegment(sketch, "E476", {"start": v(5.37, 0.27) * mm, "end": v(5.47, 0.3) * mm});
            skLineSegment(sketch, "E477", {"start": v(5.47, 0.3) * mm, "end": v(5.61, 0.24) * mm});
            skLineSegment(sketch, "E478", {"start": v(5.61, 0.24) * mm, "end": v(5.77, 0.15) * mm});
            skLineSegment(sketch, "E479", {"start": v(5.77, 0.15) * mm, "end": v(6.07, -0.1) * mm});
            skLineSegment(sketch, "E480", {"start": v(6.07, -0.1) * mm, "end": v(6.42, -0.52) * mm});
            skLineSegment(sketch, "E481", {"start": v(6.42, -0.52) * mm, "end": v(6.64, -1.02) * mm});
            skLineSegment(sketch, "E482", {"start": v(6.64, -1.02) * mm, "end": v(6.75, -1.57) * mm});
            skLineSegment(sketch, "E483", {"start": v(6.75, -1.57) * mm, "end": v(6.72, -2.23) * mm});
            skLineSegment(sketch, "E484", {"start": v(6.72, -2.23) * mm, "end": v(6.5, -2.88) * mm});
            skLineSegment(sketch, "E485", {"start": v(-0.53, -1.13) * mm, "end": v(-0.71, -1.6) * mm});
            skLineSegment(sketch, "E486", {"start": v(-0.71, -1.6) * mm, "end": v(-0.98, -2.03) * mm});
            skLineSegment(sketch, "E487", {"start": v(-0.98, -2.03) * mm, "end": v(-1.32, -2.4) * mm});
            skLineSegment(sketch, "E488", {"start": v(-1.32, -2.4) * mm, "end": v(-1.79, -2.73) * mm});
            skLineSegment(sketch, "E489", {"start": v(-1.79, -2.73) * mm, "end": v(-2.32, -2.95) * mm});
            skLineSegment(sketch, "E490", {"start": v(-2.32, -2.95) * mm, "end": v(-2.6, -3) * mm});
            skLineSegment(sketch, "E491", {"start": v(-2.6, -3) * mm, "end": v(-2.92, -3.02) * mm});
            skLineSegment(sketch, "E492", {"start": v(-2.92, -3.02) * mm, "end": v(-3.16, -3) * mm});
            skLineSegment(sketch, "E493", {"start": v(-3.16, -3) * mm, "end": v(-3.36, -2.97) * mm});
            skLineSegment(sketch, "E494", {"start": v(-3.36, -2.97) * mm, "end": v(-3.86, -2.73) * mm});
            skLineSegment(sketch, "E495", {"start": v(-3.86, -2.73) * mm, "end": v(-4.27, -2.35) * mm});
            skLineSegment(sketch, "E496", {"start": v(-4.27, -2.35) * mm, "end": v(-4.5, -1.97) * mm});
            skLineSegment(sketch, "E497", {"start": v(-4.5, -1.97) * mm, "end": v(-4.63, -1.54) * mm});
            skLineSegment(sketch, "E498", {"start": v(-4.63, -1.54) * mm, "end": v(-4.68, -1.19) * mm});
            skLineSegment(sketch, "E499", {"start": v(-4.68, -1.19) * mm, "end": v(-4.66, -0.85) * mm});
            skLineSegment(sketch, "E500", {"start": v(-4.66, -0.85) * mm, "end": v(-4.54, -0.3) * mm});
            skLineSegment(sketch, "E501", {"start": v(-4.54, -0.3) * mm, "end": v(-4.35, 0.12) * mm});
            skLineSegment(sketch, "E502", {"start": v(-4.35, 0.12) * mm, "end": v(-4.1, 0.51) * mm});
            skLineSegment(sketch, "E503", {"start": v(-4.1, 0.51) * mm, "end": v(-3.85, 0.8) * mm});
            skLineSegment(sketch, "E504", {"start": v(-3.85, 0.8) * mm, "end": v(-3.58, 1.02) * mm});
            skLineSegment(sketch, "E505", {"start": v(-3.58, 1.02) * mm, "end": v(-3.38, 1.15) * mm});
            skLineSegment(sketch, "E506", {"start": v(-3.38, 1.15) * mm, "end": v(-3.14, 1.27) * mm});
            skLineSegment(sketch, "E507", {"start": v(-3.14, 1.27) * mm, "end": v(-2.77, 1.41) * mm});
            skLineSegment(sketch, "E508", {"start": v(-2.77, 1.41) * mm, "end": v(-2.46, 1.47) * mm});
            skLineSegment(sketch, "E509", {"start": v(-2.46, 1.47) * mm, "end": v(-2.12, 1.47) * mm});
            skLineSegment(sketch, "E510", {"start": v(-2.12, 1.47) * mm, "end": v(-1.86, 1.44) * mm});
            skLineSegment(sketch, "E511", {"start": v(-1.86, 1.44) * mm, "end": v(-1.65, 1.39) * mm});
            skLineSegment(sketch, "E512", {"start": v(-1.65, 1.39) * mm, "end": v(-1.18, 1.15) * mm});
            skLineSegment(sketch, "E513", {"start": v(-1.18, 1.15) * mm, "end": v(-0.82, 0.79) * mm});
            skLineSegment(sketch, "E514", {"start": v(-0.82, 0.79) * mm, "end": v(-0.6, 0.44) * mm});
            skLineSegment(sketch, "E515", {"start": v(-0.6, 0.44) * mm, "end": v(-0.48, 0.03) * mm});
            skLineSegment(sketch, "E516", {"start": v(-0.48, 0.03) * mm, "end": v(-0.44, -0.27) * mm});
            skLineSegment(sketch, "E517", {"start": v(-0.44, -0.27) * mm, "end": v(-0.45, -0.62) * mm});
            skLineSegment(sketch, "E518", {"start": v(-0.45, -0.62) * mm, "end": v(-0.48, -0.89) * mm});
            skLineSegment(sketch, "E519", {"start": v(-0.48, -0.89) * mm, "end": v(-0.53, -1.13) * mm});
            skLineSegment(sketch, "E520", {"start": v(4.59, -0.88) * mm, "end": v(4.57, -1.38) * mm});
            skLineSegment(sketch, "E521", {"start": v(4.57, -1.38) * mm, "end": v(4.45, -1.82) * mm});
            skLineSegment(sketch, "E522", {"start": v(4.45, -1.82) * mm, "end": v(4.28, -2.13) * mm});
            skLineSegment(sketch, "E523", {"start": v(4.28, -2.13) * mm, "end": v(4.05, -2.4) * mm});
            skLineSegment(sketch, "E524", {"start": v(4.05, -2.4) * mm, "end": v(3.64, -2.71) * mm});
            skLineSegment(sketch, "E525", {"start": v(3.64, -2.71) * mm, "end": v(3.17, -2.88) * mm});
            skLineSegment(sketch, "E526", {"start": v(3.17, -2.88) * mm, "end": v(2.76, -2.92) * mm});
            skLineSegment(sketch, "E527", {"start": v(2.76, -2.92) * mm, "end": v(2.33, -2.87) * mm});
            skLineSegment(sketch, "E528", {"start": v(2.33, -2.87) * mm, "end": v(1.86, -2.7) * mm});
            skLineSegment(sketch, "E529", {"start": v(1.86, -2.7) * mm, "end": v(1.43, -2.43) * mm});
            skLineSegment(sketch, "E530", {"start": v(1.43, -2.43) * mm, "end": v(1.04, -2.07) * mm});
            skLineSegment(sketch, "E531", {"start": v(1.04, -2.07) * mm, "end": v(0.68, -1.56) * mm});
            skLineSegment(sketch, "E532", {"start": v(0.68, -1.56) * mm, "end": v(0.44, -0.97) * mm});
            skLineSegment(sketch, "E533", {"start": v(0.44, -0.97) * mm, "end": v(0.38, -0.6) * mm});
            skLineSegment(sketch, "E534", {"start": v(0.38, -0.6) * mm, "end": v(0.36, -0.22) * mm});
            skLineSegment(sketch, "E535", {"start": v(0.36, -0.22) * mm, "end": v(0.4, 0.08) * mm});
            skLineSegment(sketch, "E536", {"start": v(0.4, 0.08) * mm, "end": v(0.46, 0.34) * mm});
            skLineSegment(sketch, "E537", {"start": v(0.46, 0.34) * mm, "end": v(0.66, 0.78) * mm});
            skLineSegment(sketch, "E538", {"start": v(0.66, 0.78) * mm, "end": v(0.95, 1.12) * mm});
            skLineSegment(sketch, "E539", {"start": v(0.95, 1.12) * mm, "end": v(1.3, 1.38) * mm});
            skLineSegment(sketch, "E540", {"start": v(1.3, 1.38) * mm, "end": v(1.7, 1.54) * mm});
            skLineSegment(sketch, "E541", {"start": v(1.7, 1.54) * mm, "end": v(2.18, 1.59) * mm});
            skLineSegment(sketch, "E542", {"start": v(2.18, 1.59) * mm, "end": v(2.67, 1.52) * mm});
            skLineSegment(sketch, "E543", {"start": v(2.67, 1.52) * mm, "end": v(3.17, 1.33) * mm});
            skLineSegment(sketch, "E544", {"start": v(3.17, 1.33) * mm, "end": v(3.57, 1.07) * mm});
            skLineSegment(sketch, "E545", {"start": v(3.57, 1.07) * mm, "end": v(3.92, 0.74) * mm});
            skLineSegment(sketch, "E546", {"start": v(3.92, 0.74) * mm, "end": v(4.15, 0.44) * mm});
            skLineSegment(sketch, "E547", {"start": v(4.15, 0.44) * mm, "end": v(4.34, 0.11) * mm});
            skLineSegment(sketch, "E548", {"start": v(4.34, 0.11) * mm, "end": v(4.46, -0.16) * mm});
            skLineSegment(sketch, "E549", {"start": v(4.46, -0.16) * mm, "end": v(4.53, -0.41) * mm});
            skLineSegment(sketch, "E550", {"start": v(4.53, -0.41) * mm, "end": v(4.57, -0.63) * mm});
            skLineSegment(sketch, "E551", {"start": v(4.57, -0.63) * mm, "end": v(4.59, -0.88) * mm});
            skLineSegment(sketch, "E552", {"start": v(5.28, 0.87) * mm, "end": v(5.23, 0.8) * mm});
            skLineSegment(sketch, "E553", {"start": v(5.23, 0.8) * mm, "end": v(5.14, 0.78) * mm});
            skLineSegment(sketch, "E554", {"start": v(5.14, 0.78) * mm, "end": v(5.01, 0.8) * mm});
            skLineSegment(sketch, "E555", {"start": v(5.01, 0.8) * mm, "end": v(4.84, 0.87) * mm});
            skLineSegment(sketch, "E556", {"start": v(4.84, 0.87) * mm, "end": v(4.45, 1.1) * mm});
            skLineSegment(sketch, "E557", {"start": v(4.45, 1.1) * mm, "end": v(3.98, 1.43) * mm});
            skLineSegment(sketch, "E558", {"start": v(3.98, 1.43) * mm, "end": v(3.5, 1.83) * mm});
            skLineSegment(sketch, "E559", {"start": v(3.5, 1.83) * mm, "end": v(3.01, 2.26) * mm});
            skLineSegment(sketch, "E560", {"start": v(3.01, 2.26) * mm, "end": v(2.64, 2.63) * mm});
            skLineSegment(sketch, "E561", {"start": v(2.64, 2.63) * mm, "end": v(2.35, 2.96) * mm});
            skLineSegment(sketch, "E562", {"start": v(2.35, 2.96) * mm, "end": v(2.19, 3.17) * mm});
            skLineSegment(sketch, "E563", {"start": v(2.19, 3.17) * mm, "end": v(2.11, 3.33) * mm});
            skLineSegment(sketch, "E564", {"start": v(2.11, 3.33) * mm, "end": v(2.1, 3.4) * mm});
            skLineSegment(sketch, "E565", {"start": v(2.1, 3.4) * mm, "end": v(2.11, 3.45) * mm});
            skLineSegment(sketch, "E566", {"start": v(2.11, 3.45) * mm, "end": v(2.13, 3.48) * mm});
            skLineSegment(sketch, "E567", {"start": v(2.13, 3.48) * mm, "end": v(2.17, 3.5) * mm});
            skLineSegment(sketch, "E568", {"start": v(2.17, 3.5) * mm, "end": v(2.28, 3.52) * mm});
            skLineSegment(sketch, "E569", {"start": v(2.28, 3.52) * mm, "end": v(2.45, 3.54) * mm});
            skLineSegment(sketch, "E570", {"start": v(2.45, 3.54) * mm, "end": v(2.65, 3.55) * mm});
            skLineSegment(sketch, "E571", {"start": v(2.65, 3.55) * mm, "end": v(3.1, 3.54) * mm});
            skLineSegment(sketch, "E572", {"start": v(3.1, 3.54) * mm, "end": v(3.48, 3.48) * mm});
            skLineSegment(sketch, "E573", {"start": v(3.48, 3.48) * mm, "end": v(3.93, 3.32) * mm});
            skLineSegment(sketch, "E574", {"start": v(3.93, 3.32) * mm, "end": v(4.32, 3.09) * mm});
            skLineSegment(sketch, "E575", {"start": v(4.32, 3.09) * mm, "end": v(4.65, 2.8) * mm});
            skLineSegment(sketch, "E576", {"start": v(4.65, 2.8) * mm, "end": v(4.96, 2.37) * mm});
            skLineSegment(sketch, "E577", {"start": v(4.96, 2.37) * mm, "end": v(5.18, 1.87) * mm});
            skLineSegment(sketch, "E578", {"start": v(5.18, 1.87) * mm, "end": v(5.24, 1.58) * mm});
            skLineSegment(sketch, "E579", {"start": v(5.24, 1.58) * mm, "end": v(5.29, 1.24) * mm});
            skLineSegment(sketch, "E580", {"start": v(5.29, 1.24) * mm, "end": v(5.3, 0.98) * mm});
            skLineSegment(sketch, "E581", {"start": v(5.3, 0.98) * mm, "end": v(5.28, 0.87) * mm});
            skLineSegment(sketch, "E582", {"start": v(-2.46, 3.25) * mm, "end": v(-2.57, 3.1) * mm});
            skLineSegment(sketch, "E583", {"start": v(-2.57, 3.1) * mm, "end": v(-2.77, 2.87) * mm});
            skLineSegment(sketch, "E584", {"start": v(-2.77, 2.87) * mm, "end": v(-3.2, 2.43) * mm});
            skLineSegment(sketch, "E585", {"start": v(-3.2, 2.43) * mm, "end": v(-3.62, 2.02) * mm});
            skLineSegment(sketch, "E586", {"start": v(-3.62, 2.02) * mm, "end": v(-4.02, 1.68) * mm});
            skLineSegment(sketch, "E587", {"start": v(-4.02, 1.68) * mm, "end": v(-4.55, 1.28) * mm});
            skLineSegment(sketch, "E588", {"start": v(-4.55, 1.28) * mm, "end": v(-4.97, 1) * mm});
            skLineSegment(sketch, "E589", {"start": v(-4.97, 1) * mm, "end": v(-5.22, 0.88) * mm});
            skLineSegment(sketch, "E590", {"start": v(-5.22, 0.88) * mm, "end": v(-5.4, 0.84) * mm});
            skLineSegment(sketch, "E591", {"start": v(-5.4, 0.84) * mm, "end": v(-5.5, 0.86) * mm});
            skLineSegment(sketch, "E592", {"start": v(-5.5, 0.86) * mm, "end": v(-5.56, 0.92) * mm});
            skLineSegment(sketch, "E593", {"start": v(-5.56, 0.92) * mm, "end": v(-5.58, 1.03) * mm});
            skLineSegment(sketch, "E594", {"start": v(-5.58, 1.03) * mm, "end": v(-5.58, 1.16) * mm});
            skLineSegment(sketch, "E595", {"start": v(-5.58, 1.16) * mm, "end": v(-5.55, 1.46) * mm});
            skLineSegment(sketch, "E596", {"start": v(-5.55, 1.46) * mm, "end": v(-5.5, 1.74) * mm});
            skLineSegment(sketch, "E597", {"start": v(-5.5, 1.74) * mm, "end": v(-5.44, 1.98) * mm});
            skLineSegment(sketch, "E598", {"start": v(-5.44, 1.98) * mm, "end": v(-5.33, 2.27) * mm});
            skLineSegment(sketch, "E599", {"start": v(-5.33, 2.27) * mm, "end": v(-5.18, 2.53) * mm});
            skLineSegment(sketch, "E600", {"start": v(-5.18, 2.53) * mm, "end": v(-4.86, 2.9) * mm});
            skLineSegment(sketch, "E601", {"start": v(-4.86, 2.9) * mm, "end": v(-4.7, 3.06) * mm});
            skLineSegment(sketch, "E602", {"start": v(-4.7, 3.06) * mm, "end": v(-4.56, 3.17) * mm});
            skLineSegment(sketch, "E603", {"start": v(-4.56, 3.17) * mm, "end": v(-4.3, 3.32) * mm});
            skLineSegment(sketch, "E604", {"start": v(-4.3, 3.32) * mm, "end": v(-3.98, 3.46) * mm});
            skLineSegment(sketch, "E605", {"start": v(-3.98, 3.46) * mm, "end": v(-3.7, 3.54) * mm});
            skLineSegment(sketch, "E606", {"start": v(-3.7, 3.54) * mm, "end": v(-3.45, 3.57) * mm});
            skLineSegment(sketch, "E607", {"start": v(-3.45, 3.57) * mm, "end": v(-3.14, 3.6) * mm});
            skLineSegment(sketch, "E608", {"start": v(-3.14, 3.6) * mm, "end": v(-2.84, 3.6) * mm});
            skLineSegment(sketch, "E609", {"start": v(-2.84, 3.6) * mm, "end": v(-2.62, 3.59) * mm});
            skLineSegment(sketch, "E610", {"start": v(-2.62, 3.59) * mm, "end": v(-2.5, 3.57) * mm});
            skLineSegment(sketch, "E611", {"start": v(-2.5, 3.57) * mm, "end": v(-2.43, 3.53) * mm});
            skLineSegment(sketch, "E612", {"start": v(-2.43, 3.53) * mm, "end": v(-2.4, 3.44) * mm});
            skLineSegment(sketch, "E613", {"start": v(-2.4, 3.44) * mm, "end": v(-2.46, 3.25) * mm});
            skLineSegment(sketch, "E614", {"start": v(1.89, 3.01) * mm, "end": v(1.96, 2.83) * mm});
            skLineSegment(sketch, "E615", {"start": v(1.96, 2.83) * mm, "end": v(1.99, 2.63) * mm});
            skLineSegment(sketch, "E616", {"start": v(1.99, 2.63) * mm, "end": v(1.93, 2.35) * mm});
            skLineSegment(sketch, "E617", {"start": v(1.93, 2.35) * mm, "end": v(1.7, 2.07) * mm});
            skLineSegment(sketch, "E618", {"start": v(1.7, 2.07) * mm, "end": v(1.33, 1.85) * mm});
            skLineSegment(sketch, "E619", {"start": v(1.33, 1.85) * mm, "end": v(0.86, 1.7) * mm});
            skLineSegment(sketch, "E620", {"start": v(0.86, 1.7) * mm, "end": v(0.21, 1.6) * mm});
            skLineSegment(sketch, "E621", {"start": v(0.21, 1.6) * mm, "end": v(-0.5, 1.63) * mm});
            skLineSegment(sketch, "E622", {"start": v(-0.5, 1.63) * mm, "end": v(-0.78, 1.69) * mm});
            skLineSegment(sketch, "E623", {"start": v(-0.78, 1.69) * mm, "end": v(-1.1, 1.78) * mm});
            skLineSegment(sketch, "E624", {"start": v(-1.1, 1.78) * mm, "end": v(-1.32, 1.87) * mm});
            skLineSegment(sketch, "E625", {"start": v(-1.32, 1.87) * mm, "end": v(-1.5, 1.96) * mm});
            skLineSegment(sketch, "E626", {"start": v(-1.5, 1.96) * mm, "end": v(-1.84, 2.25) * mm});
            skLineSegment(sketch, "E627", {"start": v(-1.84, 2.25) * mm, "end": v(-1.94, 2.37) * mm});
            skLineSegment(sketch, "E628", {"start": v(-1.94, 2.37) * mm, "end": v(-2, 2.48) * mm});
            skLineSegment(sketch, "E629", {"start": v(-2, 2.48) * mm, "end": v(-2.05, 2.79) * mm});
            skLineSegment(sketch, "E630", {"start": v(-2.05, 2.79) * mm, "end": v(-2, 3.01) * mm});
            skLineSegment(sketch, "E631", {"start": v(-2, 3.01) * mm, "end": v(-1.9, 3.15) * mm});
            skLineSegment(sketch, "E632", {"start": v(-1.9, 3.15) * mm, "end": v(-1.73, 3.32) * mm});
            skLineSegment(sketch, "E633", {"start": v(-1.73, 3.32) * mm, "end": v(-1.6, 3.45) * mm});
            skLineSegment(sketch, "E634", {"start": v(-1.6, 3.45) * mm, "end": v(-1.46, 3.56) * mm});
            skLineSegment(sketch, "E635", {"start": v(-1.46, 3.56) * mm, "end": v(-1.23, 3.7) * mm});
            skLineSegment(sketch, "E636", {"start": v(-1.23, 3.7) * mm, "end": v(-0.95, 3.81) * mm});
            skLineSegment(sketch, "E637", {"start": v(-0.95, 3.81) * mm, "end": v(-0.73, 3.9) * mm});
            skLineSegment(sketch, "E638", {"start": v(-0.73, 3.9) * mm, "end": v(-0.53, 3.95) * mm});
            skLineSegment(sketch, "E639", {"start": v(-0.53, 3.95) * mm, "end": v(-0.21, 3.98) * mm});
            skLineSegment(sketch, "E640", {"start": v(-0.21, 3.98) * mm, "end": v(0.13, 3.98) * mm});
            skLineSegment(sketch, "E641", {"start": v(0.13, 3.98) * mm, "end": v(0.4, 3.95) * mm});
            skLineSegment(sketch, "E642", {"start": v(0.4, 3.95) * mm, "end": v(0.62, 3.9) * mm});
            skLineSegment(sketch, "E643", {"start": v(0.62, 3.9) * mm, "end": v(1.07, 3.7) * mm});
            skLineSegment(sketch, "E644", {"start": v(1.07, 3.7) * mm, "end": v(1.47, 3.46) * mm});
            skLineSegment(sketch, "E645", {"start": v(1.47, 3.46) * mm, "end": v(1.72, 3.24) * mm});
            skLineSegment(sketch, "E646", {"start": v(1.72, 3.24) * mm, "end": v(1.89, 3.01) * mm});
            skLineSegment(sketch, "E647", {"start": v(-1.43, 5.79) * mm, "end": v(-2.32, 6.39) * mm});
            skLineSegment(sketch, "E648", {"start": v(-2.32, 6.39) * mm, "end": v(-3.1, 6.82) * mm});
            skLineSegment(sketch, "E649", {"start": v(-3.1, 6.82) * mm, "end": v(-3.76, 7.12) * mm});
            skLineSegment(sketch, "E650", {"start": v(-3.76, 7.12) * mm, "end": v(-4.06, 7.25) * mm});
            skLineSegment(sketch, "E651", {"start": v(-4.06, 7.25) * mm, "end": v(-4.15, 7.28) * mm});
            skLineSegment(sketch, "E652", {"start": v(-4.15, 7.28) * mm, "end": v(-4.18, 7.29) * mm});
            skLineSegment(sketch, "E653", {"start": v(-4.18, 7.29) * mm, "end": v(-4.18, 7.3) * mm});
            skLineSegment(sketch, "E654", {"start": v(-4.18, 7.3) * mm, "end": v(-4.19, 7.3) * mm});
            skLineSegment(sketch, "E655", {"start": v(-4.19, 7.3) * mm, "end": v(-4.19, 7.3) * mm});
            skLineSegment(sketch, "E656", {"start": v(-4.19, 7.3) * mm, "end": v(-4.19, 7.29) * mm});
            skLineSegment(sketch, "E657", {"start": v(-4.19, 7.29) * mm, "end": v(-4.19, 7.29) * mm});
            skLineSegment(sketch, "E658", {"start": v(-4.19, 7.29) * mm, "end": v(-4.16, 7.27) * mm});
            skLineSegment(sketch, "E659", {"start": v(-4.16, 7.27) * mm, "end": v(-3.76, 7.03) * mm});
            skLineSegment(sketch, "E660", {"start": v(-3.76, 7.03) * mm, "end": v(-3.02, 6.58) * mm});
            skLineSegment(sketch, "E661", {"start": v(-3.02, 6.58) * mm, "end": v(-2.32, 6.1) * mm});
            skLineSegment(sketch, "E662", {"start": v(-2.32, 6.1) * mm, "end": v(-1.85, 5.73) * mm});
            skLineSegment(sketch, "E663", {"start": v(-1.85, 5.73) * mm, "end": v(-1.5, 5.4) * mm});
            skLineSegment(sketch, "E664", {"start": v(-1.5, 5.4) * mm, "end": v(-1.36, 5.26) * mm});
            skLineSegment(sketch, "E665", {"start": v(-1.36, 5.26) * mm, "end": v(-1.42, 5.08) * mm});
            skLineSegment(sketch, "E666", {"start": v(-1.42, 5.08) * mm, "end": v(-1.6, 4.73) * mm});
            skLineSegment(sketch, "E667", {"start": v(-1.6, 4.73) * mm, "end": v(-1.9, 4.44) * mm});
            skLineSegment(sketch, "E668", {"start": v(-1.9, 4.44) * mm, "end": v(-2.2, 4.25) * mm});
            skLineSegment(sketch, "E669", {"start": v(-2.2, 4.25) * mm, "end": v(-2.57, 4.11) * mm});
            skLineSegment(sketch, "E670", {"start": v(-2.57, 4.11) * mm, "end": v(-2.93, 4.03) * mm});
            skLineSegment(sketch, "E671", {"start": v(-2.93, 4.03) * mm, "end": v(-3.33, 3.98) * mm});
            skLineSegment(sketch, "E672", {"start": v(-3.33, 3.98) * mm, "end": v(-3.63, 3.97) * mm});
            skLineSegment(sketch, "E673", {"start": v(-3.63, 3.97) * mm, "end": v(-3.78, 3.98) * mm});
            skLineSegment(sketch, "E674", {"start": v(-3.78, 3.98) * mm, "end": v(-3.83, 4) * mm});
            skLineSegment(sketch, "E675", {"start": v(-3.83, 4) * mm, "end": v(-3.84, 4.02) * mm});
            skLineSegment(sketch, "E676", {"start": v(-3.84, 4.02) * mm, "end": v(-3.83, 4.04) * mm});
            skLineSegment(sketch, "E677", {"start": v(-3.83, 4.04) * mm, "end": v(-3.8, 4.07) * mm});
            skLineSegment(sketch, "E678", {"start": v(-3.8, 4.07) * mm, "end": v(-3.74, 4.12) * mm});
            skLineSegment(sketch, "E679", {"start": v(-3.74, 4.12) * mm, "end": v(-3.67, 4.18) * mm});
            skLineSegment(sketch, "E680", {"start": v(-3.67, 4.18) * mm, "end": v(-3.67, 4.2) * mm});
            skLineSegment(sketch, "E681", {"start": v(-3.67, 4.2) * mm, "end": v(-3.67, 4.2) * mm});
            skLineSegment(sketch, "E682", {"start": v(-3.67, 4.2) * mm, "end": v(-3.72, 4.23) * mm});
            skLineSegment(sketch, "E683", {"start": v(-3.72, 4.23) * mm, "end": v(-3.79, 4.24) * mm});
            skLineSegment(sketch, "E684", {"start": v(-3.79, 4.24) * mm, "end": v(-4, 4.27) * mm});
            skLineSegment(sketch, "E685", {"start": v(-4, 4.27) * mm, "end": v(-4.24, 4.3) * mm});
            skLineSegment(sketch, "E686", {"start": v(-4.24, 4.3) * mm, "end": v(-4.43, 4.34) * mm});
            skLineSegment(sketch, "E687", {"start": v(-4.43, 4.34) * mm, "end": v(-4.55, 4.39) * mm});
            skLineSegment(sketch, "E688", {"start": v(-4.55, 4.39) * mm, "end": v(-4.58, 4.42) * mm});
            skLineSegment(sketch, "E689", {"start": v(-4.58, 4.42) * mm, "end": v(-4.59, 4.44) * mm});
            skLineSegment(sketch, "E690", {"start": v(-4.59, 4.44) * mm, "end": v(-4.57, 4.48) * mm});
            skLineSegment(sketch, "E691", {"start": v(-4.57, 4.48) * mm, "end": v(-4.5, 4.51) * mm});
            skLineSegment(sketch, "E692", {"start": v(-4.5, 4.51) * mm, "end": v(-4.44, 4.54) * mm});
            skLineSegment(sketch, "E693", {"start": v(-4.44, 4.54) * mm, "end": v(-4.43, 4.56) * mm});
            skLineSegment(sketch, "E694", {"start": v(-4.43, 4.56) * mm, "end": v(-4.42, 4.57) * mm});
            skLineSegment(sketch, "E695", {"start": v(-4.42, 4.57) * mm, "end": v(-4.43, 4.57) * mm});
            skLineSegment(sketch, "E696", {"start": v(-4.43, 4.57) * mm, "end": v(-4.44, 4.58) * mm});
            skLineSegment(sketch, "E697", {"start": v(-4.44, 4.58) * mm, "end": v(-4.48, 4.6) * mm});
            skLineSegment(sketch, "E698", {"start": v(-4.48, 4.6) * mm, "end": v(-4.63, 4.65) * mm});
            skLineSegment(sketch, "E699", {"start": v(-4.63, 4.65) * mm, "end": v(-4.84, 4.72) * mm});
            skLineSegment(sketch, "E700", {"start": v(-4.84, 4.72) * mm, "end": v(-5.03, 4.8) * mm});
            skLineSegment(sketch, "E701", {"start": v(-5.03, 4.8) * mm, "end": v(-5.18, 4.89) * mm});
            skLineSegment(sketch, "E702", {"start": v(-5.18, 4.89) * mm, "end": v(-5.22, 4.93) * mm});
            skLineSegment(sketch, "E703", {"start": v(-5.22, 4.93) * mm, "end": v(-5.24, 4.95) * mm});
            skLineSegment(sketch, "E704", {"start": v(-5.24, 4.95) * mm, "end": v(-5.22, 4.97) * mm});
            skLineSegment(sketch, "E705", {"start": v(-5.22, 4.97) * mm, "end": v(-5.2, 4.99) * mm});
            skLineSegment(sketch, "E706", {"start": v(-5.2, 4.99) * mm, "end": v(-5.1, 5.02) * mm});
            skLineSegment(sketch, "E707", {"start": v(-5.1, 5.02) * mm, "end": v(-4.96, 5.05) * mm});
            skLineSegment(sketch, "E708", {"start": v(-4.96, 5.05) * mm, "end": v(-5.22, 5.2) * mm});
            skLineSegment(sketch, "E709", {"start": v(-5.22, 5.2) * mm, "end": v(-5.6, 5.43) * mm});
            skLineSegment(sketch, "E710", {"start": v(-5.6, 5.43) * mm, "end": v(-5.71, 5.53) * mm});
            skLineSegment(sketch, "E711", {"start": v(-5.71, 5.53) * mm, "end": v(-5.74, 5.57) * mm});
            skLineSegment(sketch, "E712", {"start": v(-5.74, 5.57) * mm, "end": v(-5.75, 5.6) * mm});
            skLineSegment(sketch, "E713", {"start": v(-5.75, 5.6) * mm, "end": v(-5.74, 5.6) * mm});
            skLineSegment(sketch, "E714", {"start": v(-5.74, 5.6) * mm, "end": v(-5.72, 5.61) * mm});
            skLineSegment(sketch, "E715", {"start": v(-5.72, 5.61) * mm, "end": v(-5.69, 5.63) * mm});
            skLineSegment(sketch, "E716", {"start": v(-5.69, 5.63) * mm, "end": v(-5.6, 5.65) * mm});
            skLineSegment(sketch, "E717", {"start": v(-5.6, 5.65) * mm, "end": v(-5.45, 5.66) * mm});
            skLineSegment(sketch, "E718", {"start": v(-5.45, 5.66) * mm, "end": v(-5.63, 5.78) * mm});
            skLineSegment(sketch, "E719", {"start": v(-5.63, 5.78) * mm, "end": v(-5.8, 5.92) * mm});
            skLineSegment(sketch, "E720", {"start": v(-5.8, 5.92) * mm, "end": v(-5.95, 6.05) * mm});
            skLineSegment(sketch, "E721", {"start": v(-5.95, 6.05) * mm, "end": v(-6.04, 6.17) * mm});
            skLineSegment(sketch, "E722", {"start": v(-6.04, 6.17) * mm, "end": v(-6.06, 6.23) * mm});
            skLineSegment(sketch, "E723", {"start": v(-6.06, 6.23) * mm, "end": v(-6.05, 6.25) * mm});
            skLineSegment(sketch, "E724", {"start": v(-6.05, 6.25) * mm, "end": v(-6.03, 6.26) * mm});
            skLineSegment(sketch, "E725", {"start": v(-6.03, 6.26) * mm, "end": v(-5.97, 6.25) * mm});
            skLineSegment(sketch, "E726", {"start": v(-5.97, 6.25) * mm, "end": v(-5.9, 6.25) * mm});
            skLineSegment(sketch, "E727", {"start": v(-5.9, 6.25) * mm, "end": v(-5.84, 6.26) * mm});
            skLineSegment(sketch, "E728", {"start": v(-5.84, 6.26) * mm, "end": v(-5.81, 6.28) * mm});
            skLineSegment(sketch, "E729", {"start": v(-5.81, 6.28) * mm, "end": v(-5.82, 6.3) * mm});
            skLineSegment(sketch, "E730", {"start": v(-5.82, 6.3) * mm, "end": v(-5.84, 6.33) * mm});
            skLineSegment(sketch, "E731", {"start": v(-5.84, 6.33) * mm, "end": v(-5.96, 6.44) * mm});
            skLineSegment(sketch, "E732", {"start": v(-5.96, 6.44) * mm, "end": v(-6.1, 6.58) * mm});
            skLineSegment(sketch, "E733", {"start": v(-6.1, 6.58) * mm, "end": v(-6.22, 6.72) * mm});
            skLineSegment(sketch, "E734", {"start": v(-6.22, 6.72) * mm, "end": v(-6.29, 6.82) * mm});
            skLineSegment(sketch, "E735", {"start": v(-6.29, 6.82) * mm, "end": v(-6.3, 6.88) * mm});
            skLineSegment(sketch, "E736", {"start": v(-6.3, 6.88) * mm, "end": v(-6.3, 6.9) * mm});
            skLineSegment(sketch, "E737", {"start": v(-6.3, 6.9) * mm, "end": v(-6.27, 6.92) * mm});
            skLineSegment(sketch, "E738", {"start": v(-6.27, 6.92) * mm, "end": v(-6.12, 6.92) * mm});
            skLineSegment(sketch, "E739", {"start": v(-6.12, 6.92) * mm, "end": v(-5.93, 6.9) * mm});
            skLineSegment(sketch, "E740", {"start": v(-5.93, 6.9) * mm, "end": v(-6.12, 7.08) * mm});
            skLineSegment(sketch, "E741", {"start": v(-6.12, 7.08) * mm, "end": v(-6.26, 7.23) * mm});
            skLineSegment(sketch, "E742", {"start": v(-6.26, 7.23) * mm, "end": v(-6.38, 7.38) * mm});
            skLineSegment(sketch, "E743", {"start": v(-6.38, 7.38) * mm, "end": v(-6.45, 7.48) * mm});
            skLineSegment(sketch, "E744", {"start": v(-6.45, 7.48) * mm, "end": v(-6.47, 7.53) * mm});
            skLineSegment(sketch, "E745", {"start": v(-6.47, 7.53) * mm, "end": v(-6.46, 7.54) * mm});
            skLineSegment(sketch, "E746", {"start": v(-6.46, 7.54) * mm, "end": v(-6.45, 7.54) * mm});
            skLineSegment(sketch, "E747", {"start": v(-6.45, 7.54) * mm, "end": v(-6.42, 7.55) * mm});
            skLineSegment(sketch, "E748", {"start": v(-6.42, 7.55) * mm, "end": v(-6.29, 7.56) * mm});
            skLineSegment(sketch, "E749", {"start": v(-6.29, 7.56) * mm, "end": v(-6.16, 7.57) * mm});
            skLineSegment(sketch, "E750", {"start": v(-6.16, 7.57) * mm, "end": v(-6.12, 7.58) * mm});
            skLineSegment(sketch, "E751", {"start": v(-6.12, 7.58) * mm, "end": v(-6.11, 7.6) * mm});
            skLineSegment(sketch, "E752", {"start": v(-6.11, 7.6) * mm, "end": v(-6.12, 7.65) * mm});
            skLineSegment(sketch, "E753", {"start": v(-6.12, 7.65) * mm, "end": v(-6.15, 7.72) * mm});
            skLineSegment(sketch, "E754", {"start": v(-6.15, 7.72) * mm, "end": v(-6.21, 7.86) * mm});
            skLineSegment(sketch, "E755", {"start": v(-6.21, 7.86) * mm, "end": v(-6.28, 7.98) * mm});
            skLineSegment(sketch, "E756", {"start": v(-6.28, 7.98) * mm, "end": v(-6.34, 8.08) * mm});
            skLineSegment(sketch, "E757", {"start": v(-6.34, 8.08) * mm, "end": v(-6.4, 8.19) * mm});
            skLineSegment(sketch, "E758", {"start": v(-6.4, 8.19) * mm, "end": v(-6.4, 8.22) * mm});
            skLineSegment(sketch, "E759", {"start": v(-6.4, 8.22) * mm, "end": v(-6.4, 8.24) * mm});
            skLineSegment(sketch, "E760", {"start": v(-6.4, 8.24) * mm, "end": v(-6.34, 8.26) * mm});
            skLineSegment(sketch, "E761", {"start": v(-6.34, 8.26) * mm, "end": v(-6.25, 8.27) * mm});
            skLineSegment(sketch, "E762", {"start": v(-6.25, 8.27) * mm, "end": v(-6, 8.28) * mm});
            skLineSegment(sketch, "E763", {"start": v(-6, 8.28) * mm, "end": v(-5.58, 8.28) * mm});
            skLineSegment(sketch, "E764", {"start": v(-5.58, 8.28) * mm, "end": v(-5.67, 8.37) * mm});
            skLineSegment(sketch, "E765", {"start": v(-5.67, 8.37) * mm, "end": v(-5.73, 8.45) * mm});
            skLineSegment(sketch, "E766", {"start": v(-5.73, 8.45) * mm, "end": v(-5.74, 8.49) * mm});
            skLineSegment(sketch, "E767", {"start": v(-5.74, 8.49) * mm, "end": v(-5.68, 8.53) * mm});
            skLineSegment(sketch, "E768", {"start": v(-5.68, 8.53) * mm, "end": v(-5.54, 8.56) * mm});
            skLineSegment(sketch, "E769", {"start": v(-5.54, 8.56) * mm, "end": v(-5.36, 8.55) * mm});
            skLineSegment(sketch, "E770", {"start": v(-5.36, 8.55) * mm, "end": v(-5.12, 8.52) * mm});
            skLineSegment(sketch, "E771", {"start": v(-5.12, 8.52) * mm, "end": v(-4.94, 8.49) * mm});
            skLineSegment(sketch, "E772", {"start": v(-4.94, 8.49) * mm, "end": v(-4.8, 8.45) * mm});
            skLineSegment(sketch, "E773", {"start": v(-4.8, 8.45) * mm, "end": v(-4.76, 8.45) * mm});
            skLineSegment(sketch, "E774", {"start": v(-4.76, 8.45) * mm, "end": v(-4.75, 8.47) * mm});
            skLineSegment(sketch, "E775", {"start": v(-4.75, 8.47) * mm, "end": v(-4.76, 8.5) * mm});
            skLineSegment(sketch, "E776", {"start": v(-4.76, 8.5) * mm, "end": v(-4.83, 8.6) * mm});
            skLineSegment(sketch, "E777", {"start": v(-4.83, 8.6) * mm, "end": v(-4.88, 8.68) * mm});
            skLineSegment(sketch, "E778", {"start": v(-4.88, 8.68) * mm, "end": v(-4.88, 8.72) * mm});
            skLineSegment(sketch, "E779", {"start": v(-4.88, 8.72) * mm, "end": v(-4.82, 8.74) * mm});
            skLineSegment(sketch, "E780", {"start": v(-4.82, 8.74) * mm, "end": v(-4.68, 8.73) * mm});
            skLineSegment(sketch, "E781", {"start": v(-4.68, 8.73) * mm, "end": v(-4.25, 8.62) * mm});
            skLineSegment(sketch, "E782", {"start": v(-4.25, 8.62) * mm, "end": v(-4.12, 8.59) * mm});
            skLineSegment(sketch, "E783", {"start": v(-4.12, 8.59) * mm, "end": v(-4.08, 8.58) * mm});
            skLineSegment(sketch, "E784", {"start": v(-4.08, 8.58) * mm, "end": v(-4.07, 8.58) * mm});
            skLineSegment(sketch, "E785", {"start": v(-4.07, 8.58) * mm, "end": v(-4.07, 8.59) * mm});
            skLineSegment(sketch, "E786", {"start": v(-4.07, 8.59) * mm, "end": v(-4.07, 8.6) * mm});
            skLineSegment(sketch, "E787", {"start": v(-4.07, 8.6) * mm, "end": v(-4.07, 8.6) * mm});
            skLineSegment(sketch, "E788", {"start": v(-4.07, 8.6) * mm, "end": v(-4.09, 8.63) * mm});
            skLineSegment(sketch, "E789", {"start": v(-4.09, 8.63) * mm, "end": v(-4.16, 8.7) * mm});
            skLineSegment(sketch, "E790", {"start": v(-4.16, 8.7) * mm, "end": v(-4.25, 8.83) * mm});
            skLineSegment(sketch, "E791", {"start": v(-4.25, 8.83) * mm, "end": v(-4.26, 8.86) * mm});
            skLineSegment(sketch, "E792", {"start": v(-4.26, 8.86) * mm, "end": v(-4.25, 8.88) * mm});
            skLineSegment(sketch, "E793", {"start": v(-4.25, 8.88) * mm, "end": v(-4.2, 8.89) * mm});
            skLineSegment(sketch, "E794", {"start": v(-4.2, 8.89) * mm, "end": v(-4.14, 8.88) * mm});
            skLineSegment(sketch, "E795", {"start": v(-4.14, 8.88) * mm, "end": v(-3.89, 8.81) * mm});
            skLineSegment(sketch, "E796", {"start": v(-3.89, 8.81) * mm, "end": v(-3.67, 8.73) * mm});
            skLineSegment(sketch, "E797", {"start": v(-3.67, 8.73) * mm, "end": v(-3.54, 8.67) * mm});
            skLineSegment(sketch, "E798", {"start": v(-3.54, 8.67) * mm, "end": v(-3.45, 8.62) * mm});
            skLineSegment(sketch, "E799", {"start": v(-3.45, 8.62) * mm, "end": v(-3.42, 8.6) * mm});
            skLineSegment(sketch, "E800", {"start": v(-3.42, 8.6) * mm, "end": v(-3.4, 8.6) * mm});
            skLineSegment(sketch, "E801", {"start": v(-3.4, 8.6) * mm, "end": v(-3.4, 8.6) * mm});
            skLineSegment(sketch, "E802", {"start": v(-3.4, 8.6) * mm, "end": v(-3.39, 8.62) * mm});
            skLineSegment(sketch, "E803", {"start": v(-3.39, 8.62) * mm, "end": v(-3.39, 8.65) * mm});
            skLineSegment(sketch, "E804", {"start": v(-3.39, 8.65) * mm, "end": v(-3.4, 8.7) * mm});
            skLineSegment(sketch, "E805", {"start": v(-3.4, 8.7) * mm, "end": v(-3.44, 8.8) * mm});
            skLineSegment(sketch, "E806", {"start": v(-3.44, 8.8) * mm, "end": v(-3.47, 8.87) * mm});
            skLineSegment(sketch, "E807", {"start": v(-3.47, 8.87) * mm, "end": v(-3.48, 8.9) * mm});
            skLineSegment(sketch, "E808", {"start": v(-3.48, 8.9) * mm, "end": v(-3.47, 8.91) * mm});
            skLineSegment(sketch, "E809", {"start": v(-3.47, 8.91) * mm, "end": v(-3.45, 8.92) * mm});
            skLineSegment(sketch, "E810", {"start": v(-3.45, 8.92) * mm, "end": v(-3.41, 8.91) * mm});
            skLineSegment(sketch, "E811", {"start": v(-3.41, 8.91) * mm, "end": v(-3.3, 8.86) * mm});
            skLineSegment(sketch, "E812", {"start": v(-3.3, 8.86) * mm, "end": v(-2.97, 8.66) * mm});
            skLineSegment(sketch, "E813", {"start": v(-2.97, 8.66) * mm, "end": v(-2.82, 8.56) * mm});
            skLineSegment(sketch, "E814", {"start": v(-2.82, 8.56) * mm, "end": v(-2.77, 8.54) * mm});
            skLineSegment(sketch, "E815", {"start": v(-2.77, 8.54) * mm, "end": v(-2.73, 8.55) * mm});
            skLineSegment(sketch, "E816", {"start": v(-2.73, 8.55) * mm, "end": v(-2.71, 8.6) * mm});
            skLineSegment(sketch, "E817", {"start": v(-2.71, 8.6) * mm, "end": v(-2.72, 8.71) * mm});
            skLineSegment(sketch, "E818", {"start": v(-2.72, 8.71) * mm, "end": v(-2.73, 8.8) * mm});
            skLineSegment(sketch, "E819", {"start": v(-2.73, 8.8) * mm, "end": v(-2.72, 8.82) * mm});
            skLineSegment(sketch, "E820", {"start": v(-2.72, 8.82) * mm, "end": v(-2.7, 8.83) * mm});
            skLineSegment(sketch, "E821", {"start": v(-2.7, 8.83) * mm, "end": v(-2.68, 8.82) * mm});
            skLineSegment(sketch, "E822", {"start": v(-2.68, 8.82) * mm, "end": v(-2.66, 8.81) * mm});
            skLineSegment(sketch, "E823", {"start": v(-2.66, 8.81) * mm, "end": v(-2.6, 8.78) * mm});
            skLineSegment(sketch, "E824", {"start": v(-2.6, 8.78) * mm, "end": v(-2.48, 8.69) * mm});
            skLineSegment(sketch, "E825", {"start": v(-2.48, 8.69) * mm, "end": v(-2.25, 8.5) * mm});
            skLineSegment(sketch, "E826", {"start": v(-2.25, 8.5) * mm, "end": v(-2.17, 8.41) * mm});
            skLineSegment(sketch, "E827", {"start": v(-2.17, 8.41) * mm, "end": v(-2.13, 8.4) * mm});
            skLineSegment(sketch, "E828", {"start": v(-2.13, 8.4) * mm, "end": v(-2.11, 8.4) * mm});
            skLineSegment(sketch, "E829", {"start": v(-2.11, 8.4) * mm, "end": v(-2.1, 8.4) * mm});
            skLineSegment(sketch, "E830", {"start": v(-2.1, 8.4) * mm, "end": v(-2.1, 8.42) * mm});
            skLineSegment(sketch, "E831", {"start": v(-2.1, 8.42) * mm, "end": v(-2.1, 8.45) * mm});
            skLineSegment(sketch, "E832", {"start": v(-2.1, 8.45) * mm, "end": v(-2.09, 8.54) * mm});
            skLineSegment(sketch, "E833", {"start": v(-2.09, 8.54) * mm, "end": v(-2.08, 8.64) * mm});
            skLineSegment(sketch, "E834", {"start": v(-2.08, 8.64) * mm, "end": v(-2.06, 8.66) * mm});
            skLineSegment(sketch, "E835", {"start": v(-2.06, 8.66) * mm, "end": v(-2.04, 8.67) * mm});
            skLineSegment(sketch, "E836", {"start": v(-2.04, 8.67) * mm, "end": v(-2, 8.65) * mm});
            skLineSegment(sketch, "E837", {"start": v(-2, 8.65) * mm, "end": v(-1.96, 8.62) * mm});
            skLineSegment(sketch, "E838", {"start": v(-1.96, 8.62) * mm, "end": v(-1.85, 8.52) * mm});
            skLineSegment(sketch, "E839", {"start": v(-1.85, 8.52) * mm, "end": v(-1.57, 8.24) * mm});
            skLineSegment(sketch, "E840", {"start": v(-1.57, 8.24) * mm, "end": v(-1.46, 8.12) * mm});
            skLineSegment(sketch, "E841", {"start": v(-1.46, 8.12) * mm, "end": v(-1.43, 8.09) * mm});
            skLineSegment(sketch, "E842", {"start": v(-1.43, 8.09) * mm, "end": v(-1.43, 8.08) * mm});
            skLineSegment(sketch, "E843", {"start": v(-1.43, 8.08) * mm, "end": v(-1.42, 8.08) * mm});
            skLineSegment(sketch, "E844", {"start": v(-1.42, 8.08) * mm, "end": v(-1.42, 8.08) * mm});
            skLineSegment(sketch, "E845", {"start": v(-1.42, 8.08) * mm, "end": v(-1.42, 8.09) * mm});
            skLineSegment(sketch, "E846", {"start": v(-1.42, 8.09) * mm, "end": v(-1.4, 8.1) * mm});
            skLineSegment(sketch, "E847", {"start": v(-1.4, 8.1) * mm, "end": v(-1.39, 8.18) * mm});
            skLineSegment(sketch, "E848", {"start": v(-1.39, 8.18) * mm, "end": v(-1.36, 8.26) * mm});
            skLineSegment(sketch, "E849", {"start": v(-1.36, 8.26) * mm, "end": v(-1.33, 8.3) * mm});
            skLineSegment(sketch, "E850", {"start": v(-1.33, 8.3) * mm, "end": v(-1.32, 8.3) * mm});
            skLineSegment(sketch, "E851", {"start": v(-1.32, 8.3) * mm, "end": v(-1.3, 8.3) * mm});
            skLineSegment(sketch, "E852", {"start": v(-1.3, 8.3) * mm, "end": v(-1.25, 8.25) * mm});
            skLineSegment(sketch, "E853", {"start": v(-1.25, 8.25) * mm, "end": v(-1.1, 8.1) * mm});
            skLineSegment(sketch, "E854", {"start": v(-1.1, 8.1) * mm, "end": v(-0.93, 7.89) * mm});
            skLineSegment(sketch, "E855", {"start": v(-0.93, 7.89) * mm, "end": v(-0.77, 7.65) * mm});
            skLineSegment(sketch, "E856", {"start": v(-0.77, 7.65) * mm, "end": v(-0.54, 7.17) * mm});
            skLineSegment(sketch, "E857", {"start": v(-0.54, 7.17) * mm, "end": v(-0.43, 6.72) * mm});
            skLineSegment(sketch, "E858", {"start": v(-0.43, 6.72) * mm, "end": v(-0.42, 6.4) * mm});
            skLineSegment(sketch, "E859", {"start": v(-0.42, 6.4) * mm, "end": v(-0.5, 6.12) * mm});
            skLineSegment(sketch, "E860", {"start": v(-0.5, 6.12) * mm, "end": v(-0.6, 5.95) * mm});
            skLineSegment(sketch, "E861", {"start": v(-0.6, 5.95) * mm, "end": v(-0.74, 5.78) * mm});
            skLineSegment(sketch, "E862", {"start": v(-0.74, 5.78) * mm, "end": v(-0.86, 5.67) * mm});
            skLineSegment(sketch, "E863", {"start": v(-0.86, 5.67) * mm, "end": v(-0.98, 5.6) * mm});
            skLineSegment(sketch, "E864", {"start": v(-0.98, 5.6) * mm, "end": v(-1.1, 5.54) * mm});
            skLineSegment(sketch, "E865", {"start": v(-1.1, 5.54) * mm, "end": v(-1.43, 5.79) * mm});
            skLineSegment(sketch, "E866", {"start": v(4.68, 4.69) * mm, "end": v(4.47, 4.61) * mm});
            skLineSegment(sketch, "E867", {"start": v(4.47, 4.61) * mm, "end": v(4.41, 4.59) * mm});
            skLineSegment(sketch, "E868", {"start": v(4.41, 4.59) * mm, "end": v(4.4, 4.58) * mm});
            skLineSegment(sketch, "E869", {"start": v(4.4, 4.58) * mm, "end": v(4.4, 4.57) * mm});
            skLineSegment(sketch, "E870", {"start": v(4.4, 4.57) * mm, "end": v(4.4, 4.56) * mm});
            skLineSegment(sketch, "E871", {"start": v(4.4, 4.56) * mm, "end": v(4.4, 4.55) * mm});
            skLineSegment(sketch, "E872", {"start": v(4.4, 4.55) * mm, "end": v(4.42, 4.54) * mm});
            skLineSegment(sketch, "E873", {"start": v(4.42, 4.54) * mm, "end": v(4.47, 4.52) * mm});
            skLineSegment(sketch, "E874", {"start": v(4.47, 4.52) * mm, "end": v(4.54, 4.48) * mm});
            skLineSegment(sketch, "E875", {"start": v(4.54, 4.48) * mm, "end": v(4.57, 4.45) * mm});
            skLineSegment(sketch, "E876", {"start": v(4.57, 4.45) * mm, "end": v(4.57, 4.43) * mm});
            skLineSegment(sketch, "E877", {"start": v(4.57, 4.43) * mm, "end": v(4.54, 4.4) * mm});
            skLineSegment(sketch, "E878", {"start": v(4.54, 4.4) * mm, "end": v(4.46, 4.36) * mm});
            skLineSegment(sketch, "E879", {"start": v(4.46, 4.36) * mm, "end": v(4.32, 4.32) * mm});
            skLineSegment(sketch, "E880", {"start": v(4.32, 4.32) * mm, "end": v(3.99, 4.27) * mm});
            skLineSegment(sketch, "E881", {"start": v(3.99, 4.27) * mm, "end": v(3.73, 4.23) * mm});
            skLineSegment(sketch, "E882", {"start": v(3.73, 4.23) * mm, "end": v(3.64, 4.2) * mm});
            skLineSegment(sketch, "E883", {"start": v(3.64, 4.2) * mm, "end": v(3.63, 4.18) * mm});
            skLineSegment(sketch, "E884", {"start": v(3.63, 4.18) * mm, "end": v(3.63, 4.17) * mm});
            skLineSegment(sketch, "E885", {"start": v(3.63, 4.17) * mm, "end": v(3.66, 4.14) * mm});
            skLineSegment(sketch, "E886", {"start": v(3.66, 4.14) * mm, "end": v(3.7, 4.12) * mm});
            skLineSegment(sketch, "E887", {"start": v(3.7, 4.12) * mm, "end": v(3.77, 4.07) * mm});
            skLineSegment(sketch, "E888", {"start": v(3.77, 4.07) * mm, "end": v(3.78, 4.05) * mm});
            skLineSegment(sketch, "E889", {"start": v(3.78, 4.05) * mm, "end": v(3.79, 4.04) * mm});
            skLineSegment(sketch, "E890", {"start": v(3.79, 4.04) * mm, "end": v(3.78, 4.01) * mm});
            skLineSegment(sketch, "E891", {"start": v(3.78, 4.01) * mm, "end": v(3.76, 3.99) * mm});
            skLineSegment(sketch, "E892", {"start": v(3.76, 3.99) * mm, "end": v(3.67, 3.97) * mm});
            skLineSegment(sketch, "E893", {"start": v(3.67, 3.97) * mm, "end": v(3.54, 3.97) * mm});
            skLineSegment(sketch, "E894", {"start": v(3.54, 3.97) * mm, "end": v(3.37, 3.97) * mm});
            skLineSegment(sketch, "E895", {"start": v(3.37, 3.97) * mm, "end": v(3.15, 4) * mm});
            skLineSegment(sketch, "E896", {"start": v(3.15, 4) * mm, "end": v(2.5, 4.12) * mm});
            skLineSegment(sketch, "E897", {"start": v(2.5, 4.12) * mm, "end": v(1.98, 4.36) * mm});
            skLineSegment(sketch, "E898", {"start": v(1.98, 4.36) * mm, "end": v(1.67, 4.6) * mm});
            skLineSegment(sketch, "E899", {"start": v(1.67, 4.6) * mm, "end": v(1.45, 4.91) * mm});
            skLineSegment(sketch, "E900", {"start": v(1.45, 4.91) * mm, "end": v(1.4, 5.04) * mm});
            skLineSegment(sketch, "E901", {"start": v(1.4, 5.04) * mm, "end": v(1.35, 5.14) * mm});
            skLineSegment(sketch, "E902", {"start": v(1.35, 5.14) * mm, "end": v(1.35, 5.25) * mm});
            skLineSegment(sketch, "E903", {"start": v(1.35, 5.25) * mm, "end": v(1.41, 5.34) * mm});
            skLineSegment(sketch, "E904", {"start": v(1.41, 5.34) * mm, "end": v(1.54, 5.47) * mm});
            skLineSegment(sketch, "E905", {"start": v(1.54, 5.47) * mm, "end": v(2, 5.88) * mm});
            skLineSegment(sketch, "E906", {"start": v(2, 5.88) * mm, "end": v(2.61, 6.33) * mm});
            skLineSegment(sketch, "E907", {"start": v(2.61, 6.33) * mm, "end": v(3.17, 6.7) * mm});
            skLineSegment(sketch, "E908", {"start": v(3.17, 6.7) * mm, "end": v(3.77, 7.06) * mm});
            skLineSegment(sketch, "E909", {"start": v(3.77, 7.06) * mm, "end": v(4.15, 7.28) * mm});
            skLineSegment(sketch, "E910", {"start": v(4.15, 7.28) * mm, "end": v(4.17, 7.3) * mm});
            skLineSegment(sketch, "E911", {"start": v(4.17, 7.3) * mm, "end": v(4.17, 7.3) * mm});
            skLineSegment(sketch, "E912", {"start": v(4.17, 7.3) * mm, "end": v(4.14, 7.3) * mm});
            skLineSegment(sketch, "E913", {"start": v(4.14, 7.3) * mm, "end": v(3.74, 7.13) * mm});
            skLineSegment(sketch, "E914", {"start": v(3.74, 7.13) * mm, "end": v(3.05, 6.81) * mm});
            skLineSegment(sketch, "E915", {"start": v(3.05, 6.81) * mm, "end": v(2.39, 6.45) * mm});
            skLineSegment(sketch, "E916", {"start": v(2.39, 6.45) * mm, "end": v(1.46, 5.83) * mm});
            skLineSegment(sketch, "E917", {"start": v(1.46, 5.83) * mm, "end": v(1.29, 5.71) * mm});
            skLineSegment(sketch, "E918", {"start": v(1.29, 5.71) * mm, "end": v(1.15, 5.62) * mm});
            skLineSegment(sketch, "E919", {"start": v(1.15, 5.62) * mm, "end": v(1.07, 5.56) * mm});
            skLineSegment(sketch, "E920", {"start": v(1.07, 5.56) * mm, "end": v(1.05, 5.55) * mm});
            skLineSegment(sketch, "E921", {"start": v(1.05, 5.55) * mm, "end": v(1.05, 5.55) * mm});
            skLineSegment(sketch, "E922", {"start": v(1.05, 5.55) * mm, "end": v(1.04, 5.55) * mm});
            skLineSegment(sketch, "E923", {"start": v(1.04, 5.55) * mm, "end": v(1, 5.57) * mm});
            skLineSegment(sketch, "E924", {"start": v(1, 5.57) * mm, "end": v(0.94, 5.6) * mm});
            skLineSegment(sketch, "E925", {"start": v(0.94, 5.6) * mm, "end": v(0.81, 5.68) * mm});
            skLineSegment(sketch, "E926", {"start": v(0.81, 5.68) * mm, "end": v(0.7, 5.77) * mm});
            skLineSegment(sketch, "E927", {"start": v(0.7, 5.77) * mm, "end": v(0.62, 5.85) * mm});
            skLineSegment(sketch, "E928", {"start": v(0.62, 5.85) * mm, "end": v(0.5, 6.02) * mm});
            skLineSegment(sketch, "E929", {"start": v(0.5, 6.02) * mm, "end": v(0.43, 6.19) * mm});
            skLineSegment(sketch, "E930", {"start": v(0.43, 6.19) * mm, "end": v(0.4, 6.35) * mm});
            skLineSegment(sketch, "E931", {"start": v(0.4, 6.35) * mm, "end": v(0.4, 6.56) * mm});
            skLineSegment(sketch, "E932", {"start": v(0.4, 6.56) * mm, "end": v(0.4, 6.76) * mm});
            skLineSegment(sketch, "E933", {"start": v(0.4, 6.76) * mm, "end": v(0.42, 6.91) * mm});
            skLineSegment(sketch, "E934", {"start": v(0.42, 6.91) * mm, "end": v(0.49, 7.15) * mm});
            skLineSegment(sketch, "E935", {"start": v(0.49, 7.15) * mm, "end": v(0.61, 7.42) * mm});
            skLineSegment(sketch, "E936", {"start": v(0.61, 7.42) * mm, "end": v(0.78, 7.72) * mm});
            skLineSegment(sketch, "E937", {"start": v(0.78, 7.72) * mm, "end": v(0.93, 7.94) * mm});
            skLineSegment(sketch, "E938", {"start": v(0.93, 7.94) * mm, "end": v(1.08, 8.14) * mm});
            skLineSegment(sketch, "E939", {"start": v(1.08, 8.14) * mm, "end": v(1.22, 8.27) * mm});
            skLineSegment(sketch, "E940", {"start": v(1.22, 8.27) * mm, "end": v(1.27, 8.3) * mm});
            skLineSegment(sketch, "E941", {"start": v(1.27, 8.3) * mm, "end": v(1.3, 8.31) * mm});
            skLineSegment(sketch, "E942", {"start": v(1.3, 8.31) * mm, "end": v(1.32, 8.3) * mm});
            skLineSegment(sketch, "E943", {"start": v(1.32, 8.3) * mm, "end": v(1.32, 8.28) * mm});
            skLineSegment(sketch, "E944", {"start": v(1.32, 8.28) * mm, "end": v(1.33, 8.25) * mm});
            skLineSegment(sketch, "E945", {"start": v(1.33, 8.25) * mm, "end": v(1.33, 8.22) * mm});
            skLineSegment(sketch, "E946", {"start": v(1.33, 8.22) * mm, "end": v(1.35, 8.16) * mm});
            skLineSegment(sketch, "E947", {"start": v(1.35, 8.16) * mm, "end": v(1.39, 8.07) * mm});
            skLineSegment(sketch, "E948", {"start": v(1.39, 8.07) * mm, "end": v(1.67, 8.37) * mm});
            skLineSegment(sketch, "E949", {"start": v(1.67, 8.37) * mm, "end": v(1.79, 8.5) * mm});
            skLineSegment(sketch, "E950", {"start": v(1.79, 8.5) * mm, "end": v(1.9, 8.6) * mm});
            skLineSegment(sketch, "E951", {"start": v(1.9, 8.6) * mm, "end": v(1.96, 8.65) * mm});
            skLineSegment(sketch, "E952", {"start": v(1.96, 8.65) * mm, "end": v(1.98, 8.66) * mm});
            skLineSegment(sketch, "E953", {"start": v(1.98, 8.66) * mm, "end": v(1.99, 8.67) * mm});
            skLineSegment(sketch, "E954", {"start": v(1.99, 8.67) * mm, "end": v(2, 8.66) * mm});
            skLineSegment(sketch, "E955", {"start": v(2, 8.66) * mm, "end": v(2.02, 8.64) * mm});
            skLineSegment(sketch, "E956", {"start": v(2.02, 8.64) * mm, "end": v(2.04, 8.56) * mm});
            skLineSegment(sketch, "E957", {"start": v(2.04, 8.56) * mm, "end": v(2.05, 8.46) * mm});
            skLineSegment(sketch, "E958", {"start": v(2.05, 8.46) * mm, "end": v(2.07, 8.4) * mm});
            skLineSegment(sketch, "E959", {"start": v(2.07, 8.4) * mm, "end": v(2.09, 8.38) * mm});
            skLineSegment(sketch, "E960", {"start": v(2.09, 8.38) * mm, "end": v(2.1, 8.38) * mm});
            skLineSegment(sketch, "E961", {"start": v(2.1, 8.38) * mm, "end": v(2.17, 8.44) * mm});
            skLineSegment(sketch, "E962", {"start": v(2.17, 8.44) * mm, "end": v(2.22, 8.5) * mm});
            skLineSegment(sketch, "E963", {"start": v(2.22, 8.5) * mm, "end": v(2.3, 8.58) * mm});
            skLineSegment(sketch, "E964", {"start": v(2.3, 8.58) * mm, "end": v(2.46, 8.7) * mm});
            skLineSegment(sketch, "E965", {"start": v(2.46, 8.7) * mm, "end": v(2.6, 8.8) * mm});
            skLineSegment(sketch, "E966", {"start": v(2.6, 8.8) * mm, "end": v(2.64, 8.82) * mm});
            skLineSegment(sketch, "E967", {"start": v(2.64, 8.82) * mm, "end": v(2.65, 8.83) * mm});
            skLineSegment(sketch, "E968", {"start": v(2.65, 8.83) * mm, "end": v(2.66, 8.82) * mm});
            skLineSegment(sketch, "E969", {"start": v(2.66, 8.82) * mm, "end": v(2.67, 8.82) * mm});
            skLineSegment(sketch, "E970", {"start": v(2.67, 8.82) * mm, "end": v(2.68, 8.79) * mm});
            skLineSegment(sketch, "E971", {"start": v(2.68, 8.79) * mm, "end": v(2.68, 8.69) * mm});
            skLineSegment(sketch, "E972", {"start": v(2.68, 8.69) * mm, "end": v(2.7, 8.57) * mm});
            skLineSegment(sketch, "E973", {"start": v(2.7, 8.57) * mm, "end": v(2.7, 8.54) * mm});
            skLineSegment(sketch, "E974", {"start": v(2.7, 8.54) * mm, "end": v(2.7, 8.53) * mm});
            skLineSegment(sketch, "E975", {"start": v(2.7, 8.53) * mm, "end": v(2.71, 8.53) * mm});
            skLineSegment(sketch, "E976", {"start": v(2.71, 8.53) * mm, "end": v(2.73, 8.53) * mm});
            skLineSegment(sketch, "E977", {"start": v(2.73, 8.53) * mm, "end": v(2.78, 8.56) * mm});
            skLineSegment(sketch, "E978", {"start": v(2.78, 8.56) * mm, "end": v(2.92, 8.65) * mm});
            skLineSegment(sketch, "E979", {"start": v(2.92, 8.65) * mm, "end": v(3.1, 8.78) * mm});
            skLineSegment(sketch, "E980", {"start": v(3.1, 8.78) * mm, "end": v(3.26, 8.87) * mm});
            skLineSegment(sketch, "E981", {"start": v(3.26, 8.87) * mm, "end": v(3.42, 8.93) * mm});
            skLineSegment(sketch, "E982", {"start": v(3.42, 8.93) * mm, "end": v(3.45, 8.92) * mm});
            skLineSegment(sketch, "E983", {"start": v(3.45, 8.92) * mm, "end": v(3.46, 8.9) * mm});
            skLineSegment(sketch, "E984", {"start": v(3.46, 8.9) * mm, "end": v(3.44, 8.84) * mm});
            skLineSegment(sketch, "E985", {"start": v(3.44, 8.84) * mm, "end": v(3.4, 8.76) * mm});
            skLineSegment(sketch, "E986", {"start": v(3.4, 8.76) * mm, "end": v(3.34, 8.67) * mm});
            skLineSegment(sketch, "E987", {"start": v(3.34, 8.67) * mm, "end": v(3.34, 8.65) * mm});
            skLineSegment(sketch, "E988", {"start": v(3.34, 8.65) * mm, "end": v(3.35, 8.63) * mm});
            skLineSegment(sketch, "E989", {"start": v(3.35, 8.63) * mm, "end": v(3.37, 8.63) * mm});
            skLineSegment(sketch, "E990", {"start": v(3.37, 8.63) * mm, "end": v(3.42, 8.63) * mm});
            skLineSegment(sketch, "E991", {"start": v(3.42, 8.63) * mm, "end": v(3.56, 8.7) * mm});
            skLineSegment(sketch, "E992", {"start": v(3.56, 8.7) * mm, "end": v(3.76, 8.79) * mm});
            skLineSegment(sketch, "E993", {"start": v(3.76, 8.79) * mm, "end": v(3.97, 8.85) * mm});
            skLineSegment(sketch, "E994", {"start": v(3.97, 8.85) * mm, "end": v(4.12, 8.88) * mm});
            skLineSegment(sketch, "E995", {"start": v(4.12, 8.88) * mm, "end": v(4.2, 8.88) * mm});
            skLineSegment(sketch, "E996", {"start": v(4.2, 8.88) * mm, "end": v(4.22, 8.86) * mm});
            skLineSegment(sketch, "E997", {"start": v(4.22, 8.86) * mm, "end": v(4.23, 8.85) * mm});
            skLineSegment(sketch, "E998", {"start": v(4.23, 8.85) * mm, "end": v(4.22, 8.83) * mm});
            skLineSegment(sketch, "E999", {"start": v(4.22, 8.83) * mm, "end": v(4.15, 8.75) * mm});
            skLineSegment(sketch, "E1000", {"start": v(4.15, 8.75) * mm, "end": v(4.07, 8.65) * mm});
            skLineSegment(sketch, "E1001", {"start": v(4.07, 8.65) * mm, "end": v(4.05, 8.6) * mm});
            skLineSegment(sketch, "E1002", {"start": v(4.05, 8.6) * mm, "end": v(4.05, 8.59) * mm});
            skLineSegment(sketch, "E1003", {"start": v(4.05, 8.59) * mm, "end": v(4.06, 8.58) * mm});
            skLineSegment(sketch, "E1004", {"start": v(4.06, 8.58) * mm, "end": v(4.08, 8.58) * mm});
            skLineSegment(sketch, "E1005", {"start": v(4.08, 8.58) * mm, "end": v(4.1, 8.58) * mm});
            skLineSegment(sketch, "E1006", {"start": v(4.1, 8.58) * mm, "end": v(4.24, 8.63) * mm});
            skLineSegment(sketch, "E1007", {"start": v(4.24, 8.63) * mm, "end": v(4.45, 8.68) * mm});
            skLineSegment(sketch, "E1008", {"start": v(4.45, 8.68) * mm, "end": v(4.62, 8.72) * mm});
            skLineSegment(sketch, "E1009", {"start": v(4.62, 8.72) * mm, "end": v(4.74, 8.75) * mm});
            skLineSegment(sketch, "E1010", {"start": v(4.74, 8.75) * mm, "end": v(4.82, 8.75) * mm});
            skLineSegment(sketch, "E1011", {"start": v(4.82, 8.75) * mm, "end": v(4.85, 8.74) * mm});
            skLineSegment(sketch, "E1012", {"start": v(4.85, 8.74) * mm, "end": v(4.86, 8.72) * mm});
            skLineSegment(sketch, "E1013", {"start": v(4.86, 8.72) * mm, "end": v(4.84, 8.69) * mm});
            skLineSegment(sketch, "E1014", {"start": v(4.84, 8.69) * mm, "end": v(4.78, 8.6) * mm});
            skLineSegment(sketch, "E1015", {"start": v(4.78, 8.6) * mm, "end": v(4.71, 8.5) * mm});
            skLineSegment(sketch, "E1016", {"start": v(4.71, 8.5) * mm, "end": v(4.7, 8.47) * mm});
            skLineSegment(sketch, "E1017", {"start": v(4.7, 8.47) * mm, "end": v(4.7, 8.46) * mm});
            skLineSegment(sketch, "E1018", {"start": v(4.7, 8.46) * mm, "end": v(4.7, 8.45) * mm});
            skLineSegment(sketch, "E1019", {"start": v(4.7, 8.45) * mm, "end": v(4.72, 8.45) * mm});
            skLineSegment(sketch, "E1020", {"start": v(4.72, 8.45) * mm, "end": v(4.77, 8.45) * mm});
            skLineSegment(sketch, "E1021", {"start": v(4.77, 8.45) * mm, "end": v(5.05, 8.52) * mm});
            skLineSegment(sketch, "E1022", {"start": v(5.05, 8.52) * mm, "end": v(5.3, 8.56) * mm});
            skLineSegment(sketch, "E1023", {"start": v(5.3, 8.56) * mm, "end": v(5.6, 8.55) * mm});
            skLineSegment(sketch, "E1024", {"start": v(5.6, 8.55) * mm, "end": v(5.67, 8.52) * mm});
            skLineSegment(sketch, "E1025", {"start": v(5.67, 8.52) * mm, "end": v(5.7, 8.5) * mm});
            skLineSegment(sketch, "E1026", {"start": v(5.7, 8.5) * mm, "end": v(5.69, 8.45) * mm});
            skLineSegment(sketch, "E1027", {"start": v(5.69, 8.45) * mm, "end": v(5.64, 8.39) * mm});
            skLineSegment(sketch, "E1028", {"start": v(5.64, 8.39) * mm, "end": v(5.59, 8.33) * mm});
            skLineSegment(sketch, "E1029", {"start": v(5.59, 8.33) * mm, "end": v(5.58, 8.31) * mm});
            skLineSegment(sketch, "E1030", {"start": v(5.58, 8.31) * mm, "end": v(5.57, 8.3) * mm});
            skLineSegment(sketch, "E1031", {"start": v(5.57, 8.3) * mm, "end": v(5.57, 8.3) * mm});
            skLineSegment(sketch, "E1032", {"start": v(5.57, 8.3) * mm, "end": v(5.58, 8.3) * mm});
            skLineSegment(sketch, "E1033", {"start": v(5.58, 8.3) * mm, "end": v(5.6, 8.3) * mm});
            skLineSegment(sketch, "E1034", {"start": v(5.6, 8.3) * mm, "end": v(5.96, 8.28) * mm});
            skLineSegment(sketch, "E1035", {"start": v(5.96, 8.28) * mm, "end": v(6.14, 8.27) * mm});
            skLineSegment(sketch, "E1036", {"start": v(6.14, 8.27) * mm, "end": v(6.27, 8.26) * mm});
            skLineSegment(sketch, "E1037", {"start": v(6.27, 8.26) * mm, "end": v(6.35, 8.25) * mm});
            skLineSegment(sketch, "E1038", {"start": v(6.35, 8.25) * mm, "end": v(6.36, 8.25) * mm});
            skLineSegment(sketch, "E1039", {"start": v(6.36, 8.25) * mm, "end": v(6.37, 8.24) * mm});
            skLineSegment(sketch, "E1040", {"start": v(6.37, 8.24) * mm, "end": v(6.37, 8.23) * mm});
            skLineSegment(sketch, "E1041", {"start": v(6.37, 8.23) * mm, "end": v(6.37, 8.21) * mm});
            skLineSegment(sketch, "E1042", {"start": v(6.37, 8.21) * mm, "end": v(6.36, 8.17) * mm});
            skLineSegment(sketch, "E1043", {"start": v(6.36, 8.17) * mm, "end": v(6.31, 8.09) * mm});
            skLineSegment(sketch, "E1044", {"start": v(6.31, 8.09) * mm, "end": v(6.16, 7.82) * mm});
            skLineSegment(sketch, "E1045", {"start": v(6.16, 7.82) * mm, "end": v(6.08, 7.63) * mm});
            skLineSegment(sketch, "E1046", {"start": v(6.08, 7.63) * mm, "end": v(6.07, 7.6) * mm});
            skLineSegment(sketch, "E1047", {"start": v(6.07, 7.6) * mm, "end": v(6.08, 7.58) * mm});
            skLineSegment(sketch, "E1048", {"start": v(6.08, 7.58) * mm, "end": v(6.1, 7.57) * mm});
            skLineSegment(sketch, "E1049", {"start": v(6.1, 7.57) * mm, "end": v(6.14, 7.56) * mm});
            skLineSegment(sketch, "E1050", {"start": v(6.14, 7.56) * mm, "end": v(6.24, 7.56) * mm});
            skLineSegment(sketch, "E1051", {"start": v(6.24, 7.56) * mm, "end": v(6.37, 7.55) * mm});
            skLineSegment(sketch, "E1052", {"start": v(6.37, 7.55) * mm, "end": v(6.4, 7.54) * mm});
            skLineSegment(sketch, "E1053", {"start": v(6.4, 7.54) * mm, "end": v(6.42, 7.52) * mm});
            skLineSegment(sketch, "E1054", {"start": v(6.42, 7.52) * mm, "end": v(6.38, 7.43) * mm});
            skLineSegment(sketch, "E1055", {"start": v(6.38, 7.43) * mm, "end": v(6.3, 7.33) * mm});
            skLineSegment(sketch, "E1056", {"start": v(6.3, 7.33) * mm, "end": v(6.09, 7.1) * mm});
            skLineSegment(sketch, "E1057", {"start": v(6.09, 7.1) * mm, "end": v(5.88, 6.9) * mm});
            skLineSegment(sketch, "E1058", {"start": v(5.88, 6.9) * mm, "end": v(6.07, 6.92) * mm});
            skLineSegment(sketch, "E1059", {"start": v(6.07, 6.92) * mm, "end": v(6.22, 6.92) * mm});
            skLineSegment(sketch, "E1060", {"start": v(6.22, 6.92) * mm, "end": v(6.26, 6.91) * mm});
            skLineSegment(sketch, "E1061", {"start": v(6.26, 6.91) * mm, "end": v(6.27, 6.91) * mm});
            skLineSegment(sketch, "E1062", {"start": v(6.27, 6.91) * mm, "end": v(6.27, 6.9) * mm});
            skLineSegment(sketch, "E1063", {"start": v(6.27, 6.9) * mm, "end": v(6.27, 6.85) * mm});
            skLineSegment(sketch, "E1064", {"start": v(6.27, 6.85) * mm, "end": v(6.2, 6.75) * mm});
            skLineSegment(sketch, "E1065", {"start": v(6.2, 6.75) * mm, "end": v(5.96, 6.48) * mm});
            skLineSegment(sketch, "E1066", {"start": v(5.96, 6.48) * mm, "end": v(5.84, 6.34) * mm});
            skLineSegment(sketch, "E1067", {"start": v(5.84, 6.34) * mm, "end": v(5.81, 6.3) * mm});
            skLineSegment(sketch, "E1068", {"start": v(5.81, 6.3) * mm, "end": v(5.8, 6.26) * mm});
            skLineSegment(sketch, "E1069", {"start": v(5.8, 6.26) * mm, "end": v(5.82, 6.25) * mm});
            skLineSegment(sketch, "E1070", {"start": v(5.82, 6.25) * mm, "end": v(5.84, 6.25) * mm});
            skLineSegment(sketch, "E1071", {"start": v(5.84, 6.25) * mm, "end": v(5.94, 6.25) * mm});
            skLineSegment(sketch, "E1072", {"start": v(5.94, 6.25) * mm, "end": v(6, 6.26) * mm});
            skLineSegment(sketch, "E1073", {"start": v(6, 6.26) * mm, "end": v(6.02, 6.24) * mm});
            skLineSegment(sketch, "E1074", {"start": v(6.02, 6.24) * mm, "end": v(6.03, 6.2) * mm});
            skLineSegment(sketch, "E1075", {"start": v(6.03, 6.2) * mm, "end": v(6, 6.16) * mm});
            skLineSegment(sketch, "E1076", {"start": v(6, 6.16) * mm, "end": v(5.97, 6.11) * mm});
            skLineSegment(sketch, "E1077", {"start": v(5.97, 6.11) * mm, "end": v(5.86, 6) * mm});
            skLineSegment(sketch, "E1078", {"start": v(5.86, 6) * mm, "end": v(5.55, 5.75) * mm});
            skLineSegment(sketch, "E1079", {"start": v(5.55, 5.75) * mm, "end": v(5.4, 5.65) * mm});
            skLineSegment(sketch, "E1080", {"start": v(5.4, 5.65) * mm, "end": v(5.55, 5.64) * mm});
            skLineSegment(sketch, "E1081", {"start": v(5.55, 5.64) * mm, "end": v(5.66, 5.62) * mm});
            skLineSegment(sketch, "E1082", {"start": v(5.66, 5.62) * mm, "end": v(5.7, 5.58) * mm});
            skLineSegment(sketch, "E1083", {"start": v(5.7, 5.58) * mm, "end": v(5.69, 5.55) * mm});
            skLineSegment(sketch, "E1084", {"start": v(5.69, 5.55) * mm, "end": v(5.66, 5.5) * mm});
            skLineSegment(sketch, "E1085", {"start": v(5.66, 5.5) * mm, "end": v(5.52, 5.4) * mm});
            skLineSegment(sketch, "E1086", {"start": v(5.52, 5.4) * mm, "end": v(5.3, 5.26) * mm});
            skLineSegment(sketch, "E1087", {"start": v(5.3, 5.26) * mm, "end": v(5.12, 5.16) * mm});
            skLineSegment(sketch, "E1088", {"start": v(5.12, 5.16) * mm, "end": v(4.9, 5.05) * mm});
            skLineSegment(sketch, "E1089", {"start": v(4.9, 5.05) * mm, "end": v(5.05, 5.02) * mm});
            skLineSegment(sketch, "E1090", {"start": v(5.05, 5.02) * mm, "end": v(5.15, 4.98) * mm});
            skLineSegment(sketch, "E1091", {"start": v(5.15, 4.98) * mm, "end": v(5.18, 4.96) * mm});
            skLineSegment(sketch, "E1092", {"start": v(5.18, 4.96) * mm, "end": v(5.19, 4.95) * mm});
            skLineSegment(sketch, "E1093", {"start": v(5.19, 4.95) * mm, "end": v(5.15, 4.9) * mm});
            skLineSegment(sketch, "E1094", {"start": v(5.15, 4.9) * mm, "end": v(5.04, 4.83) * mm});
            skLineSegment(sketch, "E1095", {"start": v(5.04, 4.83) * mm, "end": v(4.68, 4.69) * mm});
            skPoint(sketch, "E1096", {"position": v(-16.25, 89) * mm});
            skPoint(sketch, "E1097.MirrorP", {"position": v(61.75, 89) * mm});
            skPoint(sketch, "E1098", {"position": v(22.75, 89) * mm});
            skPoint(sketch, "E1099.MirrorP", {"position": v(-16.25, -89) * mm});
            skPoint(sketch, "E1100.MirrorP", {"position": v(22.75, -89) * mm});
            skPoint(sketch, "E1101.MirrorP", {"position": v(61.75, -89) * mm});
            skCircle(sketch, "E1102", {"center": v(0, -75.3) * mm, "radius": 6.6 * mm});
            skLineSegment(sketch, "E1103", {"start": v(-7.7, 74.97) * mm, "end": v(-7.7, 70.6) * mm});
            skLineSegment(sketch, "E1104", {"start": v(0.52, 74.04) * mm, "end": v(2.38, 73.2) * mm});
            skLineSegment(sketch, "E1105", {"start": v(2.38, 73.2) * mm, "end": v(7.05, 75.37) * mm});
            skLineSegment(sketch, "E1106", {"start": v(7.05, 75.37) * mm, "end": v(0.52, 78.36) * mm});
            skLineSegment(sketch, "E1107", {"start": v(0.52, 78.36) * mm, "end": v(0.52, 74.04) * mm});
            skLineSegment(sketch, "E1108", {"start": v(-0.48, 78.3) * mm, "end": v(-7.02, 75.37) * mm});
            skLineSegment(sketch, "E1109", {"start": v(-0.48, 74.04) * mm, "end": v(-0.48, 78.3) * mm});
            skLineSegment(sketch, "E1110", {"start": v(-2.32, 73.2) * mm, "end": v(-0.48, 74.04) * mm});
            skLineSegment(sketch, "E1111", {"start": v(-7.02, 75.37) * mm, "end": v(-2.32, 73.2) * mm});
            skLineSegment(sketch, "E1112", {"start": v(7.8, 70.58) * mm, "end": v(0.58, 67.43) * mm});
            skLineSegment(sketch, "E1113", {"start": v(7.8, 74.97) * mm, "end": v(7.8, 70.58) * mm});
            skLineSegment(sketch, "E1114", {"start": v(0.58, 71.62) * mm, "end": v(7.8, 74.97) * mm});
            skLineSegment(sketch, "E1115", {"start": v(0.58, 67.43) * mm, "end": v(0.58, 71.62) * mm});
            skLineSegment(sketch, "E1116", {"start": v(-0.5, 71.62) * mm, "end": v(-7.7, 74.97) * mm});
            skLineSegment(sketch, "E1117", {"start": v(-0.5, 67.39) * mm, "end": v(-0.5, 71.62) * mm});
            skLineSegment(sketch, "E1118", {"start": v(-7.7, 70.6) * mm, "end": v(-0.5, 67.39) * mm});
            const initialGuessF2  = {"E49": [-0.01, -0.04239, 1, 0, 0.0077]};
            skSetInitialGuess(sketch, initialGuessF2);
            skSolve(sketch);
        }
        {
            var Q0;
            Q0=sQuery(id+"F2.wireOp",VERTEX,"E21.MirrorP");
            var Q1;
            Q1=sQuery(id+"F2.wireOp",VERTEX,"E20");
            var Q2;
            Q2=sQuery(id+"F2.wireOp",VERTEX,"E1096");
            var Q3;
            Q3=sQuery(id+"F2.wireOp",VERTEX,"E1098");
            var Q4;
            Q4=sQuery(id+"F2.wireOp",VERTEX,"E1097.MirrorP");
            var Q5;
            Q5=sQuery(id+"F2.wireOp",VERTEX,"E1101.MirrorP");
            var Q6;
            Q6=sQuery(id+"F2.wireOp",VERTEX,"E1100.MirrorP");
            var Q7;
            Q7=sQuery(id+"F2.wireOp",VERTEX,"E1099.MirrorP");
            var Q8;
            Q8=makeQuery(id+"F1.opExtrude","SWEPT_BODY",BODY,{"disambiguationData":[OSD([sQuery(id+"F0.wireOp",EDGE,"E0.bottom"),sQuery(id+"F0.wireOp",EDGE,"E0.top"),sQuery(id+"F0.wireOp",EDGE,"E0.left"),sQuery(id+"F0.wireOp",EDGE,"E0.right"),sQuery(id+"F0.wireOp",EDGE,"E1.bottom"),sQuery(id+"F0.wireOp",EDGE,"E1.top"),sQuery(id+"F0.wireOp",EDGE,"E1.left"),sQuery(id+"F0.wireOp",EDGE,"E1.right"),sQuery(id+"F0.wireOp",EDGE,"E2.bottom"),sQuery(id+"F0.wireOp",EDGE,"E2.top"),sQuery(id+"F0.wireOp",EDGE,"E2.left"),sQuery(id+"F0.wireOp",EDGE,"E2.right"),sQuery(id+"F0.wireOp",EDGE,"E6"),sQuery(id+"F0.wireOp",EDGE,"E7.top"),sQuery(id+"F0.wireOp",EDGE,"E8.MirrorCS"),sQuery(id+"F0.wireOp",EDGE,"E11"),sQuery(id+"F0.wireOp",EDGE,"E12"),sQuery(id+"F0.wireOp",EDGE,"E13.top"),sQuery(id+"F0.wireOp",EDGE,"E14.MirrorCS"),sQuery(id+"F0.wireOp",EDGE,"E15"),sQuery(id+"F0.wireOp",EDGE,"E16"),sQuery(id+"F0.wireOp",EDGE,"E17.top"),sQuery(id+"F0.wireOp",EDGE,"E18.MirrorCS"),sQuery(id+"F0.wireOp",EDGE,"E19")])]});
            hole(context, id + "F3", {"style" : HoleStyle.SIMPLE, "endStyle" : HoleEndStyle.THROUGH, "standardTappedOrClearance" : lookupTablePath({ "fit" : "Normal", "standard" : "ISO", "size" : "M4", "type" : "Clearance" }), "standardBlindInLast" : lookupTablePath({ "fit" : "Standard", "standard" : "ISO", "size" : "M4", "type" : "Clearance" }), "holeDiameter" : 4.4 * mm, "majorDiameter" : 5 * mm, "isTappedThrough" : true, "tappedDepth" : 12 * mm, "tapClearance" : 3, "locations" : qUnion([Q0, Q1, Q2, Q3, Q4, Q5, Q6, Q7]), "scope" : qUnion([Q8])});
        }
        {
            var Q0;
            Q0=makeQuery(id+"F2.imprint","IMPRINT",FACE,{"disambiguationData":[TD([[makeQuery(id+"F2.imprint","IMPRINT",EDGE,{"derivedFrom":sQuery(id+"F2.wireOp",EDGE,"E49.sketch_text.stroke-0")}),-1.0]])]});
            var Q1;
            Q1=makeQuery(id+"F2.imprint","IMPRINT",FACE,{"disambiguationData":[TD([[makeQuery(id+"F2.imprint","IMPRINT",EDGE,{"derivedFrom":sQuery(id+"F2.wireOp",EDGE,"E49.sketch_text.stroke-6")}),-1.0]])]});
            var Q2;
            Q2=makeQuery(id+"F2.imprint","IMPRINT",FACE,{"disambiguationData":[TD([[makeQuery(id+"F2.imprint","IMPRINT",EDGE,{"derivedFrom":sQuery(id+"F2.wireOp",EDGE,"E49.sketch_text.stroke-18")}),-1.0]])]});
            var Q3;
            Q3=makeQuery(id+"F2.imprint","IMPRINT",FACE,{"disambiguationData":[TD([[makeQuery(id+"F2.imprint","IMPRINT",EDGE,{"derivedFrom":sQuery(id+"F2.wireOp",EDGE,"E50")}),-1.0]])]});
            var Q4;
            Q4=makeQuery(id+"F2.imprint","IMPRINT",FACE,{"disambiguationData":[TD([[makeQuery(id+"F2.imprint","IMPRINT",EDGE,{"derivedFrom":sQuery(id+"F2.wireOp",EDGE,"E23")}),1.0]])]});
            var Q5;
            Q5=makeQuery(id+"F2.imprint","IMPRINT",FACE,{"disambiguationData":[TD([[makeQuery(id+"F2.imprint","IMPRINT",EDGE,{"derivedFrom":sQuery(id+"F2.wireOp",EDGE,"E35")}),-1.0]])]});
            var Q6;
            Q6=makeQuery(id+"F2.imprint","IMPRINT",FACE,{"disambiguationData":[TD([[makeQuery(id+"F2.imprint","IMPRINT",EDGE,{"derivedFrom":sQuery(id+"F2.wireOp",EDGE,"E34")}),-1.0]])]});
            var Q7;
            Q7=makeQuery(id+"F2.imprint","IMPRINT",FACE,{"disambiguationData":[TD([[makeQuery(id+"F2.imprint","IMPRINT",EDGE,{"derivedFrom":sQuery(id+"F2.wireOp",EDGE,"E48")}),-1.0]])]});
            var Q8;
            Q8=makeQuery(id+"F2.imprint","IMPRINT",FACE,{"disambiguationData":[TD([[makeQuery(id+"F2.imprint","IMPRINT",EDGE,{"derivedFrom":sQuery(id+"F2.wireOp",EDGE,"E1108")}),1.0]])]});
            var Q9;
            Q9=makeQuery(id+"F2.imprint","IMPRINT",FACE,{"disambiguationData":[TD([[makeQuery(id+"F2.imprint","IMPRINT",EDGE,{"derivedFrom":sQuery(id+"F2.wireOp",EDGE,"E1104")}),1.0]])]});
            var Q10;
            Q10=makeQuery(id+"F2.imprint","IMPRINT",FACE,{"disambiguationData":[TD([[makeQuery(id+"F2.imprint","IMPRINT",EDGE,{"derivedFrom":sQuery(id+"F2.wireOp",EDGE,"E1112")}),-1.0]])]});
            var Q11;
            Q11=makeQuery(id+"F2.imprint","IMPRINT",FACE,{"disambiguationData":[TD([[makeQuery(id+"F2.imprint","IMPRINT",EDGE,{"derivedFrom":sQuery(id+"F2.wireOp",EDGE,"E1103")}),1.0]])]});
            extrude(context, id + "F4", {"entities" : qUnion([Q0, Q1, Q2, Q3, Q4, Q5, Q6, Q7, Q8, Q9, Q10, Q11]), "operationType" : NewBodyOperationType.REMOVE, "oppositeDirection" : true, "depth" : 2.5 * mm, "offsetDistance" : 25 * mm});
        }
        {
            var Q0;
            Q0=makeQuery(id+"F1.opExtrude","CAP_EDGE",EDGE,{"disambiguationData":[OSD([sQuery(id+"F0.wireOp",EDGE,"E0.bottom")])],"isStart":false});
            var Q1;
            Q1=makeQuery(id+"F1.opExtrude","CAP_EDGE",EDGE,{"disambiguationData":[OSD([sQuery(id+"F0.wireOp",EDGE,"E0.left")])],"isStart":false});
            var Q2;
            Q2=makeQuery(id+"F1.opExtrude","CAP_EDGE",EDGE,{"disambiguationData":[OSD([sQuery(id+"F0.wireOp",EDGE,"E0.top")])],"isStart":false});
            var Q3;
            Q3=makeQuery(id+"F1.opExtrude","CAP_EDGE",EDGE,{"disambiguationData":[OSD([sQuery(id+"F0.wireOp",EDGE,"E0.right")])],"isStart":false});
            fillet(context, id + "F5", {"entities" : qUnion([Q0, Q1, Q2, Q3]), "radius" : 2.5 * mm, "tangentPropagation" : true, "rho" : 0.5, "crossSection" : FilletCrossSection.CONIC, "allowEdgeOverflow" : false});
        }
    });
